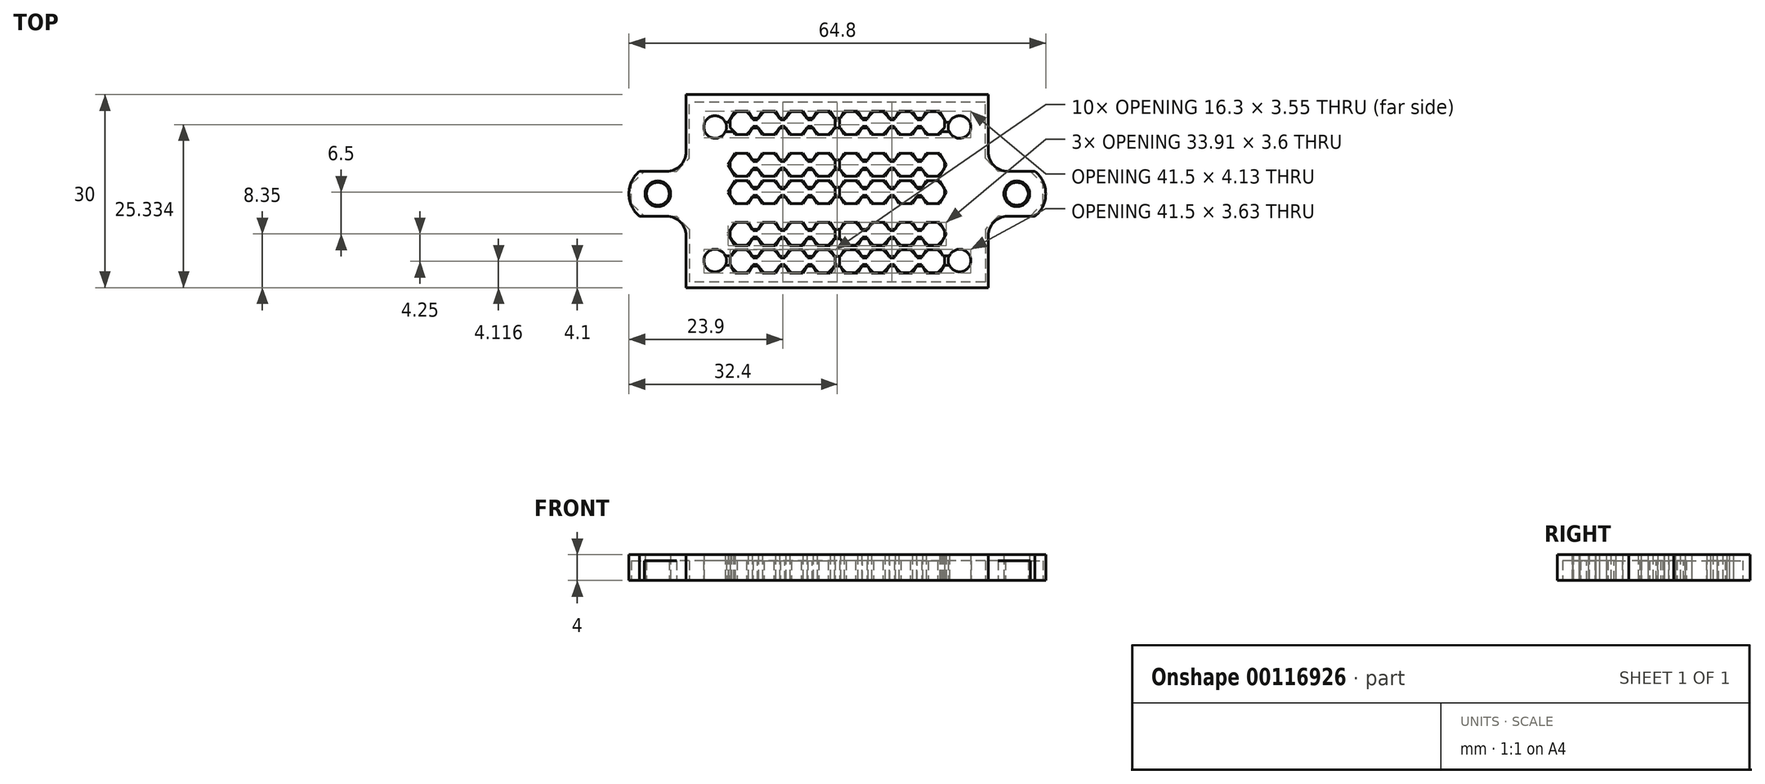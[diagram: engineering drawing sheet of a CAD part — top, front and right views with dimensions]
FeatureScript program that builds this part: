
annotation { "Feature Type Name" : "Feature", "Feature Type Description" : "" }
export const myFeature = defineFeature(function(context is Context, id is Id, definition is map)
    precondition{}
    {
        {
            var Q0;
            Q0=qCreatedBy(makeId("Top.planeOp"),FACE);
            var sketch = newSketch(context, id + "F0", { "sketchPlane" : qUnion([Q0])});
            skCircle(sketch, "E0", {"center": v(-19, 10.38) * mm, "radius": 1.77 * mm});
            skCircle(sketch, "E1.MirrorC", {"center": v(-19, -10.38) * mm, "radius": 1.77 * mm});
            skCircle(sketch, "E2.MirrorC", {"center": v(19, 10.38) * mm, "radius": 1.77 * mm});
            skCircle(sketch, "E3.MirrorC", {"center": v(19, -10.38) * mm, "radius": 1.77 * mm});
            skCircle(sketch, "E4", {"center": v(-27.9, 0) * mm, "radius": 1.77 * mm});
            skCircle(sketch, "E5.MirrorC", {"center": v(27.9, 0) * mm, "radius": 1.77 * mm});
            skLineSegment(sketch, "E6", {"start": v(-14.88, 11) * mm, "end": v(14.88, 11) * mm, "construction": true});
            skCircle(sketch, "E7.cCircle", {"center": v(-14.88, 11) * mm, "radius": 1.77 * mm, "construction": true});
            skLineSegment(sketch, "E7.0", {"start": v(-15.61, 12.77) * mm, "end": v(-14.14, 12.77) * mm});
            skLineSegment(sketch, "E7.1", {"start": v(-14.14, 12.78) * mm, "end": v(-13.1, 11.74) * mm});
            skLineSegment(sketch, "E7.2", {"start": v(-13.1, 11.74) * mm, "end": v(-13.1, 10.26) * mm});
            skLineSegment(sketch, "E7.3", {"start": v(-13.1, 10.26) * mm, "end": v(-14.14, 9.22) * mm});
            skLineSegment(sketch, "E7.4", {"start": v(-14.14, 9.22) * mm, "end": v(-15.61, 9.22) * mm});
            skLineSegment(sketch, "E7.5", {"start": v(-15.61, 9.22) * mm, "end": v(-16.65, 10.26) * mm});
            skLineSegment(sketch, "E7.6", {"start": v(-16.65, 10.26) * mm, "end": v(-16.65, 11.74) * mm});
            skLineSegment(sketch, "E7.7", {"start": v(-16.65, 11.74) * mm, "end": v(-15.61, 12.78) * mm});
            skPoint(sketch, "E7.0.midPoint", {"position": v(-14.88, 12.77) * mm});
            skLineSegment(sketch, "E8.1.0.0", {"start": v(-11.36, 12.77) * mm, "end": v(-9.89, 12.77) * mm});
            skLineSegment(sketch, "E8.1.0.1", {"start": v(-9.89, 12.78) * mm, "end": v(-8.85, 11.74) * mm});
            skLineSegment(sketch, "E8.1.0.2", {"start": v(-8.85, 11.74) * mm, "end": v(-8.85, 10.26) * mm});
            skLineSegment(sketch, "E8.1.0.3", {"start": v(-8.85, 10.26) * mm, "end": v(-9.89, 9.22) * mm});
            skLineSegment(sketch, "E8.1.0.4", {"start": v(-9.89, 9.22) * mm, "end": v(-11.36, 9.22) * mm});
            skLineSegment(sketch, "E8.1.0.5", {"start": v(-11.36, 9.22) * mm, "end": v(-12.4, 10.26) * mm});
            skLineSegment(sketch, "E8.1.0.6", {"start": v(-12.4, 10.26) * mm, "end": v(-12.4, 11.74) * mm});
            skLineSegment(sketch, "E8.1.0.7", {"start": v(-12.4, 11.74) * mm, "end": v(-11.36, 12.78) * mm});
            skLineSegment(sketch, "E8.2.0.0", {"start": v(-7.11, 12.77) * mm, "end": v(-5.64, 12.77) * mm});
            skLineSegment(sketch, "E8.2.0.1", {"start": v(-5.64, 12.78) * mm, "end": v(-4.6, 11.74) * mm});
            skLineSegment(sketch, "E8.2.0.2", {"start": v(-4.6, 11.74) * mm, "end": v(-4.6, 10.26) * mm});
            skLineSegment(sketch, "E8.2.0.3", {"start": v(-4.6, 10.26) * mm, "end": v(-5.64, 9.22) * mm});
            skLineSegment(sketch, "E8.2.0.4", {"start": v(-5.64, 9.22) * mm, "end": v(-7.11, 9.22) * mm});
            skLineSegment(sketch, "E8.2.0.5", {"start": v(-7.11, 9.22) * mm, "end": v(-8.15, 10.26) * mm});
            skLineSegment(sketch, "E8.2.0.6", {"start": v(-8.15, 10.26) * mm, "end": v(-8.15, 11.74) * mm});
            skLineSegment(sketch, "E8.2.0.7", {"start": v(-8.15, 11.74) * mm, "end": v(-7.11, 12.78) * mm});
            skLineSegment(sketch, "E8.3.0.0", {"start": v(-2.86, 12.77) * mm, "end": v(-1.39, 12.77) * mm});
            skLineSegment(sketch, "E8.3.0.1", {"start": v(-1.39, 12.78) * mm, "end": v(-0.35, 11.74) * mm});
            skLineSegment(sketch, "E8.3.0.2", {"start": v(-0.35, 11.74) * mm, "end": v(-0.35, 10.26) * mm});
            skLineSegment(sketch, "E8.3.0.3", {"start": v(-0.35, 10.26) * mm, "end": v(-1.39, 9.22) * mm});
            skLineSegment(sketch, "E8.3.0.4", {"start": v(-1.39, 9.22) * mm, "end": v(-2.86, 9.22) * mm});
            skLineSegment(sketch, "E8.3.0.5", {"start": v(-2.86, 9.22) * mm, "end": v(-3.9, 10.26) * mm});
            skLineSegment(sketch, "E8.3.0.6", {"start": v(-3.9, 10.26) * mm, "end": v(-3.9, 11.74) * mm});
            skLineSegment(sketch, "E8.3.0.7", {"start": v(-3.9, 11.74) * mm, "end": v(-2.86, 12.78) * mm});
            skLineSegment(sketch, "E8.4.0.0", {"start": v(1.39, 12.77) * mm, "end": v(2.86, 12.77) * mm});
            skLineSegment(sketch, "E8.4.0.1", {"start": v(2.86, 12.78) * mm, "end": v(3.9, 11.74) * mm});
            skLineSegment(sketch, "E8.4.0.2", {"start": v(3.9, 11.74) * mm, "end": v(3.9, 10.26) * mm});
            skLineSegment(sketch, "E8.4.0.3", {"start": v(3.9, 10.26) * mm, "end": v(2.86, 9.22) * mm});
            skLineSegment(sketch, "E8.4.0.4", {"start": v(2.86, 9.22) * mm, "end": v(1.39, 9.22) * mm});
            skLineSegment(sketch, "E8.4.0.5", {"start": v(1.39, 9.22) * mm, "end": v(0.35, 10.26) * mm});
            skLineSegment(sketch, "E8.4.0.6", {"start": v(0.35, 10.26) * mm, "end": v(0.35, 11.74) * mm});
            skLineSegment(sketch, "E8.4.0.7", {"start": v(0.35, 11.74) * mm, "end": v(1.39, 12.78) * mm});
            skLineSegment(sketch, "E8.5.0.0", {"start": v(5.64, 12.77) * mm, "end": v(7.11, 12.77) * mm});
            skLineSegment(sketch, "E8.5.0.1", {"start": v(7.11, 12.78) * mm, "end": v(8.15, 11.74) * mm});
            skLineSegment(sketch, "E8.5.0.2", {"start": v(8.15, 11.74) * mm, "end": v(8.15, 10.26) * mm});
            skLineSegment(sketch, "E8.5.0.3", {"start": v(8.15, 10.26) * mm, "end": v(7.11, 9.22) * mm});
            skLineSegment(sketch, "E8.5.0.4", {"start": v(7.11, 9.22) * mm, "end": v(5.64, 9.22) * mm});
            skLineSegment(sketch, "E8.5.0.5", {"start": v(5.64, 9.22) * mm, "end": v(4.6, 10.26) * mm});
            skLineSegment(sketch, "E8.5.0.6", {"start": v(4.6, 10.26) * mm, "end": v(4.6, 11.74) * mm});
            skLineSegment(sketch, "E8.5.0.7", {"start": v(4.6, 11.74) * mm, "end": v(5.64, 12.78) * mm});
            skLineSegment(sketch, "E8.6.0.0", {"start": v(9.89, 12.77) * mm, "end": v(11.36, 12.77) * mm});
            skLineSegment(sketch, "E8.6.0.1", {"start": v(11.36, 12.78) * mm, "end": v(12.4, 11.74) * mm});
            skLineSegment(sketch, "E8.6.0.2", {"start": v(12.4, 11.74) * mm, "end": v(12.4, 10.26) * mm});
            skLineSegment(sketch, "E8.6.0.3", {"start": v(12.4, 10.26) * mm, "end": v(11.36, 9.22) * mm});
            skLineSegment(sketch, "E8.6.0.4", {"start": v(11.36, 9.22) * mm, "end": v(9.89, 9.22) * mm});
            skLineSegment(sketch, "E8.6.0.5", {"start": v(9.89, 9.22) * mm, "end": v(8.85, 10.26) * mm});
            skLineSegment(sketch, "E8.6.0.6", {"start": v(8.85, 10.26) * mm, "end": v(8.85, 11.74) * mm});
            skLineSegment(sketch, "E8.6.0.7", {"start": v(8.85, 11.74) * mm, "end": v(9.89, 12.78) * mm});
            skLineSegment(sketch, "E8.7.0.0", {"start": v(14.14, 12.77) * mm, "end": v(15.61, 12.77) * mm});
            skLineSegment(sketch, "E8.7.0.1", {"start": v(15.61, 12.78) * mm, "end": v(16.65, 11.74) * mm});
            skLineSegment(sketch, "E8.7.0.2", {"start": v(16.65, 11.74) * mm, "end": v(16.65, 10.26) * mm});
            skLineSegment(sketch, "E8.7.0.3", {"start": v(16.65, 10.26) * mm, "end": v(15.61, 9.22) * mm});
            skLineSegment(sketch, "E8.7.0.4", {"start": v(15.61, 9.22) * mm, "end": v(14.14, 9.22) * mm});
            skLineSegment(sketch, "E8.7.0.5", {"start": v(14.14, 9.22) * mm, "end": v(13.1, 10.26) * mm});
            skLineSegment(sketch, "E8.7.0.6", {"start": v(13.1, 10.26) * mm, "end": v(13.1, 11.74) * mm});
            skLineSegment(sketch, "E8.7.0.7", {"start": v(13.1, 11.74) * mm, "end": v(14.14, 12.78) * mm});
            skLineSegment(sketch, "E8.direction1", {"start": v(-15.61, 12.77) * mm, "end": v(-11.36, 12.77) * mm, "construction": true});
            skPoint(sketch, "E9.0.1.0", {"position": v(-14.88, 2.02) * mm});
            skLineSegment(sketch, "E9.0.1.1", {"start": v(16.65, -0.49) * mm, "end": v(15.61, -1.53) * mm});
            skLineSegment(sketch, "E9.0.1.2", {"start": v(8.15, -0.49) * mm, "end": v(7.11, -1.53) * mm});
            skLineSegment(sketch, "E9.0.1.3", {"start": v(7.11, 2.03) * mm, "end": v(8.15, 0.99) * mm});
            skLineSegment(sketch, "E9.0.1.4", {"start": v(-2.86, 2.02) * mm, "end": v(-1.39, 2.02) * mm});
            skLineSegment(sketch, "E9.0.1.5", {"start": v(3.9, -0.49) * mm, "end": v(2.86, -1.53) * mm});
            skLineSegment(sketch, "E9.0.1.6", {"start": v(-4.6, -0.49) * mm, "end": v(-5.64, -1.53) * mm});
            skLineSegment(sketch, "E9.0.1.7", {"start": v(-9.89, -1.53) * mm, "end": v(-11.36, -1.53) * mm});
            skLineSegment(sketch, "E9.0.1.8", {"start": v(5.64, 2.02) * mm, "end": v(7.11, 2.02) * mm});
            skLineSegment(sketch, "E9.0.1.9", {"start": v(8.85, -0.49) * mm, "end": v(8.85, 0.99) * mm});
            skLineSegment(sketch, "E9.0.1.10", {"start": v(14.14, -1.53) * mm, "end": v(13.1, -0.49) * mm});
            skLineSegment(sketch, "E9.0.1.11", {"start": v(0.35, -0.49) * mm, "end": v(0.35, 0.99) * mm});
            skLineSegment(sketch, "E9.0.1.12", {"start": v(-7.11, 2.02) * mm, "end": v(-5.64, 2.02) * mm});
            skLineSegment(sketch, "E9.0.1.13", {"start": v(-16.65, 0.99) * mm, "end": v(-15.61, 2.02) * mm});
            skLineSegment(sketch, "E9.0.1.14", {"start": v(4.6, 0.99) * mm, "end": v(5.64, 2.02) * mm});
            skLineSegment(sketch, "E9.0.1.15", {"start": v(12.4, 0.99) * mm, "end": v(12.4, -0.49) * mm});
            skLineSegment(sketch, "E9.0.1.16", {"start": v(3.9, 0.99) * mm, "end": v(3.9, -0.49) * mm});
            skLineSegment(sketch, "E9.0.1.17", {"start": v(-8.85, 0.99) * mm, "end": v(-8.85, -0.49) * mm});
            skLineSegment(sketch, "E9.0.1.18", {"start": v(15.61, 2.03) * mm, "end": v(16.65, 0.99) * mm});
            skLineSegment(sketch, "E9.0.1.19", {"start": v(-0.35, -0.49) * mm, "end": v(-1.39, -1.53) * mm});
            skLineSegment(sketch, "E9.0.1.20", {"start": v(1.39, 2.02) * mm, "end": v(2.86, 2.02) * mm});
            skLineSegment(sketch, "E9.0.1.21", {"start": v(16.65, 0.99) * mm, "end": v(16.65, -0.49) * mm});
            skLineSegment(sketch, "E9.0.1.22", {"start": v(9.89, 2.02) * mm, "end": v(11.36, 2.02) * mm});
            skLineSegment(sketch, "E9.0.1.23", {"start": v(2.86, 2.03) * mm, "end": v(3.9, 0.99) * mm});
            skLineSegment(sketch, "E9.0.1.24", {"start": v(13.1, 0.99) * mm, "end": v(14.14, 2.02) * mm});
            skLineSegment(sketch, "E9.0.1.25", {"start": v(15.61, -1.53) * mm, "end": v(14.14, -1.53) * mm});
            skLineSegment(sketch, "E9.0.1.26", {"start": v(-1.39, -1.53) * mm, "end": v(-2.86, -1.53) * mm});
            skLineSegment(sketch, "E9.0.1.27", {"start": v(-0.35, 0.99) * mm, "end": v(-0.35, -0.49) * mm});
            skLineSegment(sketch, "E9.0.1.28", {"start": v(11.36, 2.03) * mm, "end": v(12.4, 0.99) * mm});
            skLineSegment(sketch, "E9.0.1.29", {"start": v(-3.9, -0.49) * mm, "end": v(-3.9, 0.99) * mm});
            skLineSegment(sketch, "E9.0.1.30", {"start": v(-15.61, -1.53) * mm, "end": v(-16.65, -0.49) * mm});
            skLineSegment(sketch, "E9.0.1.31", {"start": v(-16.65, -0.49) * mm, "end": v(-16.65, 0.99) * mm});
            skLineSegment(sketch, "E9.0.1.32", {"start": v(-5.64, 2.03) * mm, "end": v(-4.6, 0.99) * mm});
            skLineSegment(sketch, "E9.0.1.33", {"start": v(-9.89, 2.03) * mm, "end": v(-8.85, 0.99) * mm});
            skLineSegment(sketch, "E9.0.1.34", {"start": v(-3.9, 0.99) * mm, "end": v(-2.86, 2.02) * mm});
            skLineSegment(sketch, "E9.0.1.35", {"start": v(14.14, 2.02) * mm, "end": v(15.61, 2.02) * mm});
            skLineSegment(sketch, "E9.0.1.36", {"start": v(8.15, 0.99) * mm, "end": v(8.15, -0.49) * mm});
            skLineSegment(sketch, "E9.0.1.37", {"start": v(12.4, -0.49) * mm, "end": v(11.36, -1.53) * mm});
            skLineSegment(sketch, "E9.0.1.38", {"start": v(-1.39, 2.03) * mm, "end": v(-0.35, 0.99) * mm});
            skLineSegment(sketch, "E9.0.1.39", {"start": v(7.11, -1.53) * mm, "end": v(5.64, -1.53) * mm});
            skLineSegment(sketch, "E9.0.1.40", {"start": v(-14.14, 2.03) * mm, "end": v(-13.1, 0.99) * mm});
            skLineSegment(sketch, "E9.0.1.41", {"start": v(-4.6, 0.99) * mm, "end": v(-4.6, -0.49) * mm});
            skLineSegment(sketch, "E9.0.1.42", {"start": v(11.36, -1.53) * mm, "end": v(9.89, -1.53) * mm});
            skLineSegment(sketch, "E9.0.1.43", {"start": v(-5.64, -1.53) * mm, "end": v(-7.11, -1.53) * mm});
            skLineSegment(sketch, "E9.0.1.44", {"start": v(2.86, -1.53) * mm, "end": v(1.39, -1.53) * mm});
            skLineSegment(sketch, "E9.0.1.45", {"start": v(-8.15, -0.49) * mm, "end": v(-8.15, 0.99) * mm});
            skLineSegment(sketch, "E9.0.1.46", {"start": v(-2.86, -1.53) * mm, "end": v(-3.9, -0.49) * mm});
            skLineSegment(sketch, "E9.0.1.47", {"start": v(8.85, 0.99) * mm, "end": v(9.89, 2.02) * mm});
            skLineSegment(sketch, "E9.0.1.48", {"start": v(13.1, -0.49) * mm, "end": v(13.1, 0.99) * mm});
            skLineSegment(sketch, "E9.0.1.49", {"start": v(0.35, 0.99) * mm, "end": v(1.39, 2.02) * mm});
            skLineSegment(sketch, "E9.0.1.50", {"start": v(4.6, -0.49) * mm, "end": v(4.6, 0.99) * mm});
            skLineSegment(sketch, "E9.0.1.51", {"start": v(-8.15, 0.99) * mm, "end": v(-7.11, 2.02) * mm});
            skLineSegment(sketch, "E9.0.1.52", {"start": v(-13.1, 0.99) * mm, "end": v(-13.1, -0.49) * mm});
            skLineSegment(sketch, "E9.0.1.53", {"start": v(-7.11, -1.53) * mm, "end": v(-8.15, -0.49) * mm});
            skLineSegment(sketch, "E9.0.1.54", {"start": v(-15.61, 2.02) * mm, "end": v(-14.14, 2.02) * mm});
            skLineSegment(sketch, "E9.0.1.55", {"start": v(-12.4, 0.99) * mm, "end": v(-11.36, 2.02) * mm});
            skLineSegment(sketch, "E9.0.1.56", {"start": v(-11.36, 2.02) * mm, "end": v(-9.89, 2.02) * mm});
            skLineSegment(sketch, "E9.0.1.57", {"start": v(-14.14, -1.53) * mm, "end": v(-15.61, -1.53) * mm});
            skLineSegment(sketch, "E9.0.1.58", {"start": v(-8.85, -0.49) * mm, "end": v(-9.89, -1.53) * mm});
            skLineSegment(sketch, "E9.0.1.59", {"start": v(-13.1, -0.49) * mm, "end": v(-14.14, -1.53) * mm});
            skLineSegment(sketch, "E9.0.1.60", {"start": v(9.89, -1.53) * mm, "end": v(8.85, -0.49) * mm});
            skLineSegment(sketch, "E9.0.1.61", {"start": v(1.39, -1.53) * mm, "end": v(0.35, -0.49) * mm});
            skLineSegment(sketch, "E9.0.1.62", {"start": v(-11.36, -1.53) * mm, "end": v(-12.4, -0.49) * mm});
            skLineSegment(sketch, "E9.0.1.63", {"start": v(5.64, -1.53) * mm, "end": v(4.6, -0.49) * mm});
            skLineSegment(sketch, "E9.0.1.64", {"start": v(-12.4, -0.49) * mm, "end": v(-12.4, 0.99) * mm});
            skPoint(sketch, "E9.0.2.0", {"position": v(-14.88, -8.73) * mm});
            skLineSegment(sketch, "E9.0.2.1", {"start": v(16.65, -11.24) * mm, "end": v(15.61, -12.28) * mm});
            skLineSegment(sketch, "E9.0.2.2", {"start": v(8.15, -11.24) * mm, "end": v(7.11, -12.28) * mm});
            skLineSegment(sketch, "E9.0.2.3", {"start": v(7.11, -8.72) * mm, "end": v(8.15, -9.76) * mm});
            skLineSegment(sketch, "E9.0.2.4", {"start": v(-2.86, -8.73) * mm, "end": v(-1.39, -8.73) * mm});
            skLineSegment(sketch, "E9.0.2.5", {"start": v(3.9, -11.24) * mm, "end": v(2.86, -12.28) * mm});
            skLineSegment(sketch, "E9.0.2.6", {"start": v(-4.6, -11.24) * mm, "end": v(-5.64, -12.28) * mm});
            skLineSegment(sketch, "E9.0.2.7", {"start": v(-9.89, -12.28) * mm, "end": v(-11.36, -12.28) * mm});
            skLineSegment(sketch, "E9.0.2.8", {"start": v(5.64, -8.73) * mm, "end": v(7.11, -8.73) * mm});
            skLineSegment(sketch, "E9.0.2.9", {"start": v(8.85, -11.24) * mm, "end": v(8.85, -9.76) * mm});
            skLineSegment(sketch, "E9.0.2.10", {"start": v(14.14, -12.28) * mm, "end": v(13.1, -11.24) * mm});
            skLineSegment(sketch, "E9.0.2.11", {"start": v(0.35, -11.24) * mm, "end": v(0.35, -9.76) * mm});
            skLineSegment(sketch, "E9.0.2.12", {"start": v(-7.11, -8.73) * mm, "end": v(-5.64, -8.73) * mm});
            skLineSegment(sketch, "E9.0.2.13", {"start": v(-16.65, -9.76) * mm, "end": v(-15.61, -8.73) * mm});
            skLineSegment(sketch, "E9.0.2.14", {"start": v(4.6, -9.76) * mm, "end": v(5.64, -8.73) * mm});
            skLineSegment(sketch, "E9.0.2.15", {"start": v(12.4, -9.76) * mm, "end": v(12.4, -11.24) * mm});
            skLineSegment(sketch, "E9.0.2.16", {"start": v(3.9, -9.76) * mm, "end": v(3.9, -11.24) * mm});
            skLineSegment(sketch, "E9.0.2.17", {"start": v(-8.85, -9.76) * mm, "end": v(-8.85, -11.24) * mm});
            skLineSegment(sketch, "E9.0.2.18", {"start": v(15.61, -8.72) * mm, "end": v(16.65, -9.76) * mm});
            skLineSegment(sketch, "E9.0.2.19", {"start": v(-0.35, -11.24) * mm, "end": v(-1.39, -12.28) * mm});
            skLineSegment(sketch, "E9.0.2.20", {"start": v(1.39, -8.73) * mm, "end": v(2.86, -8.73) * mm});
            skLineSegment(sketch, "E9.0.2.21", {"start": v(16.65, -9.76) * mm, "end": v(16.65, -11.24) * mm});
            skLineSegment(sketch, "E9.0.2.22", {"start": v(9.89, -8.73) * mm, "end": v(11.36, -8.73) * mm});
            skLineSegment(sketch, "E9.0.2.23", {"start": v(2.86, -8.72) * mm, "end": v(3.9, -9.76) * mm});
            skLineSegment(sketch, "E9.0.2.24", {"start": v(13.1, -9.76) * mm, "end": v(14.14, -8.73) * mm});
            skLineSegment(sketch, "E9.0.2.25", {"start": v(15.61, -12.28) * mm, "end": v(14.14, -12.28) * mm});
            skLineSegment(sketch, "E9.0.2.26", {"start": v(-1.39, -12.28) * mm, "end": v(-2.86, -12.28) * mm});
            skLineSegment(sketch, "E9.0.2.27", {"start": v(-0.35, -9.76) * mm, "end": v(-0.35, -11.24) * mm});
            skLineSegment(sketch, "E9.0.2.28", {"start": v(11.36, -8.72) * mm, "end": v(12.4, -9.76) * mm});
            skLineSegment(sketch, "E9.0.2.29", {"start": v(-3.9, -11.24) * mm, "end": v(-3.9, -9.76) * mm});
            skLineSegment(sketch, "E9.0.2.30", {"start": v(-15.61, -12.28) * mm, "end": v(-16.65, -11.24) * mm});
            skLineSegment(sketch, "E9.0.2.31", {"start": v(-16.65, -11.24) * mm, "end": v(-16.65, -9.76) * mm});
            skLineSegment(sketch, "E9.0.2.32", {"start": v(-5.64, -8.72) * mm, "end": v(-4.6, -9.76) * mm});
            skLineSegment(sketch, "E9.0.2.33", {"start": v(-9.89, -8.72) * mm, "end": v(-8.85, -9.76) * mm});
            skLineSegment(sketch, "E9.0.2.34", {"start": v(-3.9, -9.76) * mm, "end": v(-2.86, -8.73) * mm});
            skLineSegment(sketch, "E9.0.2.35", {"start": v(14.14, -8.73) * mm, "end": v(15.61, -8.73) * mm});
            skLineSegment(sketch, "E9.0.2.36", {"start": v(8.15, -9.76) * mm, "end": v(8.15, -11.24) * mm});
            skLineSegment(sketch, "E9.0.2.37", {"start": v(12.4, -11.24) * mm, "end": v(11.36, -12.28) * mm});
            skLineSegment(sketch, "E9.0.2.38", {"start": v(-1.39, -8.72) * mm, "end": v(-0.35, -9.76) * mm});
            skLineSegment(sketch, "E9.0.2.39", {"start": v(7.11, -12.28) * mm, "end": v(5.64, -12.28) * mm});
            skLineSegment(sketch, "E9.0.2.40", {"start": v(-14.14, -8.72) * mm, "end": v(-13.1, -9.76) * mm});
            skLineSegment(sketch, "E9.0.2.41", {"start": v(-4.6, -9.76) * mm, "end": v(-4.6, -11.24) * mm});
            skLineSegment(sketch, "E9.0.2.42", {"start": v(11.36, -12.28) * mm, "end": v(9.89, -12.28) * mm});
            skLineSegment(sketch, "E9.0.2.43", {"start": v(-5.64, -12.28) * mm, "end": v(-7.11, -12.28) * mm});
            skLineSegment(sketch, "E9.0.2.44", {"start": v(2.86, -12.28) * mm, "end": v(1.39, -12.28) * mm});
            skLineSegment(sketch, "E9.0.2.45", {"start": v(-8.15, -11.24) * mm, "end": v(-8.15, -9.76) * mm});
            skLineSegment(sketch, "E9.0.2.46", {"start": v(-2.86, -12.28) * mm, "end": v(-3.9, -11.24) * mm});
            skLineSegment(sketch, "E9.0.2.47", {"start": v(8.85, -9.76) * mm, "end": v(9.89, -8.73) * mm});
            skLineSegment(sketch, "E9.0.2.48", {"start": v(13.1, -11.24) * mm, "end": v(13.1, -9.76) * mm});
            skLineSegment(sketch, "E9.0.2.49", {"start": v(0.35, -9.76) * mm, "end": v(1.39, -8.73) * mm});
            skLineSegment(sketch, "E9.0.2.50", {"start": v(4.6, -11.24) * mm, "end": v(4.6, -9.76) * mm});
            skLineSegment(sketch, "E9.0.2.51", {"start": v(-8.15, -9.76) * mm, "end": v(-7.11, -8.73) * mm});
            skLineSegment(sketch, "E9.0.2.52", {"start": v(-13.1, -9.76) * mm, "end": v(-13.1, -11.24) * mm});
            skLineSegment(sketch, "E9.0.2.53", {"start": v(-7.11, -12.28) * mm, "end": v(-8.15, -11.24) * mm});
            skLineSegment(sketch, "E9.0.2.54", {"start": v(-15.61, -8.73) * mm, "end": v(-14.14, -8.73) * mm});
            skLineSegment(sketch, "E9.0.2.55", {"start": v(-12.4, -9.76) * mm, "end": v(-11.36, -8.73) * mm});
            skLineSegment(sketch, "E9.0.2.56", {"start": v(-11.36, -8.73) * mm, "end": v(-9.89, -8.73) * mm});
            skLineSegment(sketch, "E9.0.2.57", {"start": v(-14.14, -12.28) * mm, "end": v(-15.61, -12.28) * mm});
            skLineSegment(sketch, "E9.0.2.58", {"start": v(-8.85, -11.24) * mm, "end": v(-9.89, -12.28) * mm});
            skLineSegment(sketch, "E9.0.2.59", {"start": v(-13.1, -11.24) * mm, "end": v(-14.14, -12.28) * mm});
            skLineSegment(sketch, "E9.0.2.60", {"start": v(9.89, -12.28) * mm, "end": v(8.85, -11.24) * mm});
            skLineSegment(sketch, "E9.0.2.61", {"start": v(1.39, -12.28) * mm, "end": v(0.35, -11.24) * mm});
            skLineSegment(sketch, "E9.0.2.62", {"start": v(-11.36, -12.28) * mm, "end": v(-12.4, -11.24) * mm});
            skLineSegment(sketch, "E9.0.2.63", {"start": v(5.64, -12.28) * mm, "end": v(4.6, -11.24) * mm});
            skLineSegment(sketch, "E9.0.2.64", {"start": v(-12.4, -11.24) * mm, "end": v(-12.4, -9.76) * mm});
            skLineSegment(sketch, "E9.direction1", {"start": v(-15.61, 9.22) * mm, "end": v(9.39, 9.22) * mm, "construction": true});
            skLineSegment(sketch, "E9.direction2", {"start": v(-15.61, 9.22) * mm, "end": v(-15.61, -1.53) * mm, "construction": true});
            skPoint(sketch, "E10.0.1.0", {"position": v(-14.88, -4.48) * mm});
            skPoint(sketch, "E10.0.1.1", {"position": v(-14.88, 6.27) * mm});
            skLineSegment(sketch, "E10.0.1.2", {"start": v(-15.61, 6.27) * mm, "end": v(-14.14, 6.27) * mm});
            skLineSegment(sketch, "E10.0.1.3", {"start": v(-13.1, 5.24) * mm, "end": v(-13.1, 3.76) * mm});
            skLineSegment(sketch, "E10.0.1.4", {"start": v(-7.11, -8.03) * mm, "end": v(-8.15, -6.99) * mm});
            skLineSegment(sketch, "E10.0.1.5", {"start": v(-7.11, 2.72) * mm, "end": v(-8.15, 3.76) * mm});
            skLineSegment(sketch, "E10.0.1.6", {"start": v(12.4, 3.76) * mm, "end": v(11.36, 2.72) * mm});
            skLineSegment(sketch, "E10.0.1.7", {"start": v(16.65, 5.24) * mm, "end": v(16.65, 3.76) * mm});
            skLineSegment(sketch, "E10.0.1.8", {"start": v(3.9, -6.99) * mm, "end": v(2.86, -8.03) * mm});
            skLineSegment(sketch, "E10.0.1.9", {"start": v(12.4, -6.99) * mm, "end": v(11.36, -8.03) * mm});
            skLineSegment(sketch, "E10.0.1.10", {"start": v(16.65, -5.51) * mm, "end": v(16.65, -6.99) * mm});
            skLineSegment(sketch, "E10.0.1.11", {"start": v(8.15, -6.99) * mm, "end": v(7.11, -8.03) * mm});
            skLineSegment(sketch, "E10.0.1.12", {"start": v(8.15, 3.76) * mm, "end": v(7.11, 2.72) * mm});
            skLineSegment(sketch, "E10.0.1.13", {"start": v(15.61, 6.28) * mm, "end": v(16.65, 5.24) * mm});
            skLineSegment(sketch, "E10.0.1.14", {"start": v(4.6, -6.99) * mm, "end": v(4.6, -5.51) * mm});
            skLineSegment(sketch, "E10.0.1.15", {"start": v(-3.9, -5.51) * mm, "end": v(-2.86, -4.48) * mm});
            skLineSegment(sketch, "E10.0.1.16", {"start": v(15.61, -4.47) * mm, "end": v(16.65, -5.51) * mm});
            skLineSegment(sketch, "E10.0.1.17", {"start": v(3.9, 3.76) * mm, "end": v(2.86, 2.72) * mm});
            skLineSegment(sketch, "E10.0.1.18", {"start": v(14.14, -4.48) * mm, "end": v(15.61, -4.48) * mm});
            skLineSegment(sketch, "E10.0.1.19", {"start": v(-0.35, -6.99) * mm, "end": v(-1.39, -8.03) * mm});
            skLineSegment(sketch, "E10.0.1.20", {"start": v(7.11, -4.47) * mm, "end": v(8.15, -5.51) * mm});
            skLineSegment(sketch, "E10.0.1.21", {"start": v(-8.15, 5.24) * mm, "end": v(-7.11, 6.27) * mm});
            skLineSegment(sketch, "E10.0.1.22", {"start": v(-0.35, 3.76) * mm, "end": v(-1.39, 2.72) * mm});
            skLineSegment(sketch, "E10.0.1.23", {"start": v(7.11, 6.28) * mm, "end": v(8.15, 5.24) * mm});
            skLineSegment(sketch, "E10.0.1.24", {"start": v(-8.15, -5.51) * mm, "end": v(-7.11, -4.48) * mm});
            skLineSegment(sketch, "E10.0.1.25", {"start": v(14.14, 6.27) * mm, "end": v(15.61, 6.27) * mm});
            skLineSegment(sketch, "E10.0.1.26", {"start": v(4.6, 3.76) * mm, "end": v(4.6, 5.24) * mm});
            skLineSegment(sketch, "E10.0.1.27", {"start": v(-3.9, 5.24) * mm, "end": v(-2.86, 6.27) * mm});
            skLineSegment(sketch, "E10.0.1.28", {"start": v(-5.64, 6.28) * mm, "end": v(-4.6, 5.24) * mm});
            skLineSegment(sketch, "E10.0.1.29", {"start": v(13.1, 3.76) * mm, "end": v(13.1, 5.24) * mm});
            skLineSegment(sketch, "E10.0.1.30", {"start": v(13.1, -6.99) * mm, "end": v(13.1, -5.51) * mm});
            skLineSegment(sketch, "E10.0.1.31", {"start": v(12.4, -5.51) * mm, "end": v(12.4, -6.99) * mm});
            skLineSegment(sketch, "E10.0.1.32", {"start": v(5.64, 2.72) * mm, "end": v(4.6, 3.76) * mm});
            skLineSegment(sketch, "E10.0.1.33", {"start": v(5.64, -8.03) * mm, "end": v(4.6, -6.99) * mm});
            skLineSegment(sketch, "E10.0.1.34", {"start": v(8.85, 5.24) * mm, "end": v(9.89, 6.27) * mm});
            skLineSegment(sketch, "E10.0.1.35", {"start": v(12.4, 5.24) * mm, "end": v(12.4, 3.76) * mm});
            skLineSegment(sketch, "E10.0.1.36", {"start": v(-8.15, -6.99) * mm, "end": v(-8.15, -5.51) * mm});
            skLineSegment(sketch, "E10.0.1.37", {"start": v(0.35, -5.51) * mm, "end": v(1.39, -4.48) * mm});
            skLineSegment(sketch, "E10.0.1.38", {"start": v(-8.85, -5.51) * mm, "end": v(-8.85, -6.99) * mm});
            skLineSegment(sketch, "E10.0.1.39", {"start": v(-9.89, 6.28) * mm, "end": v(-8.85, 5.24) * mm});
            skLineSegment(sketch, "E10.0.1.40", {"start": v(-8.85, 5.24) * mm, "end": v(-8.85, 3.76) * mm});
            skLineSegment(sketch, "E10.0.1.41", {"start": v(-16.65, -6.99) * mm, "end": v(-16.65, -5.51) * mm});
            skLineSegment(sketch, "E10.0.1.42", {"start": v(16.65, -6.99) * mm, "end": v(15.61, -8.03) * mm});
            skLineSegment(sketch, "E10.0.1.43", {"start": v(0.35, 5.24) * mm, "end": v(1.39, 6.27) * mm});
            skLineSegment(sketch, "E10.0.1.44", {"start": v(16.65, 3.76) * mm, "end": v(15.61, 2.72) * mm});
            skLineSegment(sketch, "E10.0.1.45", {"start": v(-9.89, -4.47) * mm, "end": v(-8.85, -5.51) * mm});
            skLineSegment(sketch, "E10.0.1.46", {"start": v(-12.4, -6.99) * mm, "end": v(-12.4, -5.51) * mm});
            skLineSegment(sketch, "E10.0.1.47", {"start": v(-5.64, -4.47) * mm, "end": v(-4.6, -5.51) * mm});
            skLineSegment(sketch, "E10.0.1.48", {"start": v(-12.4, 3.76) * mm, "end": v(-12.4, 5.24) * mm});
            skLineSegment(sketch, "E10.0.1.49", {"start": v(-3.9, 3.76) * mm, "end": v(-3.9, 5.24) * mm});
            skLineSegment(sketch, "E10.0.1.50", {"start": v(-16.65, -5.51) * mm, "end": v(-15.61, -4.48) * mm});
            skLineSegment(sketch, "E10.0.1.51", {"start": v(-8.15, 3.76) * mm, "end": v(-8.15, 5.24) * mm});
            skLineSegment(sketch, "E10.0.1.52", {"start": v(1.39, -8.03) * mm, "end": v(0.35, -6.99) * mm});
            skLineSegment(sketch, "E10.0.1.53", {"start": v(-16.65, 5.24) * mm, "end": v(-15.61, 6.27) * mm});
            skLineSegment(sketch, "E10.0.1.54", {"start": v(9.89, -8.03) * mm, "end": v(8.85, -6.99) * mm});
            skLineSegment(sketch, "E10.0.1.55", {"start": v(11.36, -4.47) * mm, "end": v(12.4, -5.51) * mm});
            skLineSegment(sketch, "E10.0.1.56", {"start": v(2.86, -8.03) * mm, "end": v(1.39, -8.03) * mm});
            skLineSegment(sketch, "E10.0.1.57", {"start": v(-7.11, -4.48) * mm, "end": v(-5.64, -4.48) * mm});
            skLineSegment(sketch, "E10.0.1.58", {"start": v(2.86, 2.72) * mm, "end": v(1.39, 2.72) * mm});
            skLineSegment(sketch, "E10.0.1.59", {"start": v(-3.9, -6.99) * mm, "end": v(-3.9, -5.51) * mm});
            skLineSegment(sketch, "E10.0.1.60", {"start": v(1.39, 2.72) * mm, "end": v(0.35, 3.76) * mm});
            skLineSegment(sketch, "E10.0.1.61", {"start": v(9.89, 2.72) * mm, "end": v(8.85, 3.76) * mm});
            skLineSegment(sketch, "E10.0.1.62", {"start": v(11.36, 6.28) * mm, "end": v(12.4, 5.24) * mm});
            skLineSegment(sketch, "E10.0.1.63", {"start": v(-7.11, 6.27) * mm, "end": v(-5.64, 6.27) * mm});
            skLineSegment(sketch, "E10.0.1.64", {"start": v(-13.1, -6.99) * mm, "end": v(-14.14, -8.03) * mm});
            skLineSegment(sketch, "E10.0.1.65", {"start": v(-5.64, -8.03) * mm, "end": v(-7.11, -8.03) * mm});
            skLineSegment(sketch, "E10.0.1.66", {"start": v(-0.35, 5.24) * mm, "end": v(-0.35, 3.76) * mm});
            skLineSegment(sketch, "E10.0.1.67", {"start": v(-0.35, -5.51) * mm, "end": v(-0.35, -6.99) * mm});
            skLineSegment(sketch, "E10.0.1.68", {"start": v(0.35, -6.99) * mm, "end": v(0.35, -5.51) * mm});
            skLineSegment(sketch, "E10.0.1.69", {"start": v(-13.1, 3.76) * mm, "end": v(-14.14, 2.72) * mm});
            skLineSegment(sketch, "E10.0.1.70", {"start": v(-5.64, 2.72) * mm, "end": v(-7.11, 2.72) * mm});
            skLineSegment(sketch, "E10.0.1.71", {"start": v(0.35, 3.76) * mm, "end": v(0.35, 5.24) * mm});
            skLineSegment(sketch, "E10.0.1.72", {"start": v(-15.61, -4.48) * mm, "end": v(-14.14, -4.48) * mm});
            skLineSegment(sketch, "E10.0.1.73", {"start": v(-9.89, -8.03) * mm, "end": v(-11.36, -8.03) * mm});
            skLineSegment(sketch, "E10.0.1.74", {"start": v(-4.6, 5.24) * mm, "end": v(-4.6, 3.76) * mm});
            skLineSegment(sketch, "E10.0.1.75", {"start": v(-11.36, 6.27) * mm, "end": v(-9.89, 6.27) * mm});
            skLineSegment(sketch, "E10.0.1.76", {"start": v(13.1, 5.24) * mm, "end": v(14.14, 6.27) * mm});
            skLineSegment(sketch, "E10.0.1.77", {"start": v(11.36, 2.72) * mm, "end": v(9.89, 2.72) * mm});
            skLineSegment(sketch, "E10.0.1.78", {"start": v(-12.4, -5.51) * mm, "end": v(-11.36, -4.48) * mm});
            skLineSegment(sketch, "E10.0.1.79", {"start": v(-4.6, 3.76) * mm, "end": v(-5.64, 2.72) * mm});
            skLineSegment(sketch, "E10.0.1.80", {"start": v(8.85, 3.76) * mm, "end": v(8.85, 5.24) * mm});
            skLineSegment(sketch, "E10.0.1.81", {"start": v(-14.14, 2.72) * mm, "end": v(-15.61, 2.72) * mm});
            skLineSegment(sketch, "E10.0.1.82", {"start": v(-13.1, -5.51) * mm, "end": v(-13.1, -6.99) * mm});
            skLineSegment(sketch, "E10.0.1.83", {"start": v(8.15, 5.24) * mm, "end": v(8.15, 3.76) * mm});
            skLineSegment(sketch, "E10.0.1.84", {"start": v(-4.6, -6.99) * mm, "end": v(-5.64, -8.03) * mm});
            skLineSegment(sketch, "E10.0.1.85", {"start": v(-1.39, 2.72) * mm, "end": v(-2.86, 2.72) * mm});
            skLineSegment(sketch, "E10.0.1.86", {"start": v(-1.39, 6.28) * mm, "end": v(-0.35, 5.24) * mm});
            skLineSegment(sketch, "E10.0.1.87", {"start": v(2.86, 6.28) * mm, "end": v(3.9, 5.24) * mm});
            skLineSegment(sketch, "E10.0.1.88", {"start": v(-8.85, 3.76) * mm, "end": v(-9.89, 2.72) * mm});
            skLineSegment(sketch, "E10.0.1.89", {"start": v(14.14, 2.72) * mm, "end": v(13.1, 3.76) * mm});
            skLineSegment(sketch, "E10.0.1.90", {"start": v(-1.39, -4.47) * mm, "end": v(-0.35, -5.51) * mm});
            skLineSegment(sketch, "E10.0.1.91", {"start": v(-8.85, -6.99) * mm, "end": v(-9.89, -8.03) * mm});
            skLineSegment(sketch, "E10.0.1.92", {"start": v(7.11, 2.72) * mm, "end": v(5.64, 2.72) * mm});
            skLineSegment(sketch, "E10.0.1.93", {"start": v(15.61, 2.72) * mm, "end": v(14.14, 2.72) * mm});
            skLineSegment(sketch, "E10.0.1.94", {"start": v(-2.86, 6.27) * mm, "end": v(-1.39, 6.27) * mm});
            skLineSegment(sketch, "E10.0.1.95", {"start": v(-1.39, -8.03) * mm, "end": v(-2.86, -8.03) * mm});
            skLineSegment(sketch, "E10.0.1.96", {"start": v(-11.36, -4.48) * mm, "end": v(-9.89, -4.48) * mm});
            skLineSegment(sketch, "E10.0.1.97", {"start": v(1.39, -4.48) * mm, "end": v(2.86, -4.48) * mm});
            skLineSegment(sketch, "E10.0.1.98", {"start": v(5.64, 6.27) * mm, "end": v(7.11, 6.27) * mm});
            skLineSegment(sketch, "E10.0.1.99", {"start": v(-9.89, 2.72) * mm, "end": v(-11.36, 2.72) * mm});
            skLineSegment(sketch, "E10.0.1.100", {"start": v(-12.4, 5.24) * mm, "end": v(-11.36, 6.27) * mm});
            skLineSegment(sketch, "E10.0.1.101", {"start": v(1.39, 6.27) * mm, "end": v(2.86, 6.27) * mm});
            skLineSegment(sketch, "E10.0.1.102", {"start": v(9.89, 6.27) * mm, "end": v(11.36, 6.27) * mm});
            skLineSegment(sketch, "E10.0.1.103", {"start": v(8.85, -6.99) * mm, "end": v(8.85, -5.51) * mm});
            skLineSegment(sketch, "E10.0.1.104", {"start": v(8.15, -5.51) * mm, "end": v(8.15, -6.99) * mm});
            skLineSegment(sketch, "E10.0.1.105", {"start": v(9.89, -4.48) * mm, "end": v(11.36, -4.48) * mm});
            skLineSegment(sketch, "E10.0.1.106", {"start": v(11.36, -8.03) * mm, "end": v(9.89, -8.03) * mm});
            skLineSegment(sketch, "E10.0.1.107", {"start": v(5.64, -4.48) * mm, "end": v(7.11, -4.48) * mm});
            skLineSegment(sketch, "E10.0.1.108", {"start": v(14.14, -8.03) * mm, "end": v(13.1, -6.99) * mm});
            skLineSegment(sketch, "E10.0.1.109", {"start": v(2.86, -4.47) * mm, "end": v(3.9, -5.51) * mm});
            skLineSegment(sketch, "E10.0.1.110", {"start": v(7.11, -8.03) * mm, "end": v(5.64, -8.03) * mm});
            skLineSegment(sketch, "E10.0.1.111", {"start": v(15.61, -8.03) * mm, "end": v(14.14, -8.03) * mm});
            skLineSegment(sketch, "E10.0.1.112", {"start": v(-4.6, -5.51) * mm, "end": v(-4.6, -6.99) * mm});
            skLineSegment(sketch, "E10.0.1.113", {"start": v(-14.14, -8.03) * mm, "end": v(-15.61, -8.03) * mm});
            skLineSegment(sketch, "E10.0.1.114", {"start": v(4.6, 5.24) * mm, "end": v(5.64, 6.27) * mm});
            skLineSegment(sketch, "E10.0.1.115", {"start": v(4.6, -5.51) * mm, "end": v(5.64, -4.48) * mm});
            skLineSegment(sketch, "E10.0.1.116", {"start": v(-11.36, 2.72) * mm, "end": v(-12.4, 3.76) * mm});
            skLineSegment(sketch, "E10.0.1.117", {"start": v(-2.86, 2.72) * mm, "end": v(-3.9, 3.76) * mm});
            skLineSegment(sketch, "E10.0.1.118", {"start": v(-15.61, 2.72) * mm, "end": v(-16.65, 3.76) * mm});
            skLineSegment(sketch, "E10.0.1.119", {"start": v(-11.36, -8.03) * mm, "end": v(-12.4, -6.99) * mm});
            skLineSegment(sketch, "E10.0.1.120", {"start": v(-2.86, -8.03) * mm, "end": v(-3.9, -6.99) * mm});
            skLineSegment(sketch, "E10.0.1.121", {"start": v(-15.61, -8.03) * mm, "end": v(-16.65, -6.99) * mm});
            skLineSegment(sketch, "E10.0.1.122", {"start": v(13.1, -5.51) * mm, "end": v(14.14, -4.48) * mm});
            skLineSegment(sketch, "E10.0.1.123", {"start": v(-2.86, -4.48) * mm, "end": v(-1.39, -4.48) * mm});
            skLineSegment(sketch, "E10.0.1.124", {"start": v(-16.65, 3.76) * mm, "end": v(-16.65, 5.24) * mm});
            skLineSegment(sketch, "E10.0.1.125", {"start": v(8.85, -5.51) * mm, "end": v(9.89, -4.48) * mm});
            skLineSegment(sketch, "E10.0.1.126", {"start": v(3.9, 5.24) * mm, "end": v(3.9, 3.76) * mm});
            skLineSegment(sketch, "E10.0.1.127", {"start": v(3.9, -5.51) * mm, "end": v(3.9, -6.99) * mm});
            skLineSegment(sketch, "E10.0.1.128", {"start": v(-14.14, 6.28) * mm, "end": v(-13.1, 5.24) * mm});
            skLineSegment(sketch, "E10.0.1.129", {"start": v(-14.14, -4.47) * mm, "end": v(-13.1, -5.51) * mm});
            skLineSegment(sketch, "E10.direction1", {"start": v(-15.61, -12.28) * mm, "end": v(9.39, -12.28) * mm, "construction": true});
            skLineSegment(sketch, "E10.direction2", {"start": v(-15.61, -12.28) * mm, "end": v(-15.61, -8.03) * mm, "construction": true});
            skLineSegment(sketch, "E11.bottom", {"start": v(23, -13.75) * mm, "end": v(-23, -13.75) * mm});
            skLineSegment(sketch, "E11.top", {"start": v(23, 14.25) * mm, "end": v(-23, 14.25) * mm});
            skLineSegment(sketch, "E11.left", {"start": v(32, -3.5) * mm, "end": v(32, 3.5) * mm});
            skLineSegment(sketch, "E11.right", {"start": v(-32, -3.5) * mm, "end": v(-32, 3.5) * mm});
            skPoint(sketch, "E11.middle", {"position": v(0, 0.25) * mm});
            skPoint(sketch, "E11.middle.positionSnap0", {"position": v(0.35, 0.25) * mm});
            skPoint(sketch, "E11.centerSnap0", {"position": v(0.35, 0.25) * mm});
            skLineSegment(sketch, "E12", {"start": v(-32, 3.5) * mm, "end": v(-23, 3.5) * mm});
            skLineSegment(sketch, "E13", {"start": v(-23, 3.5) * mm, "end": v(-23, 14.25) * mm});
            skLineSegment(sketch, "E14.MirrorCS", {"start": v(23, 3.5) * mm, "end": v(23, 14.25) * mm});
            skLineSegment(sketch, "E15.MirrorCS", {"start": v(32, 3.5) * mm, "end": v(23, 3.5) * mm});
            skLineSegment(sketch, "E16.MirrorCS", {"start": v(32, -3.5) * mm, "end": v(23, -3.5) * mm});
            skLineSegment(sketch, "E17.MirrorCS", {"start": v(23, -3.5) * mm, "end": v(23, -13.75) * mm});
            skLineSegment(sketch, "E18.MirrorCS", {"start": v(-32, -3.5) * mm, "end": v(-23, -3.5) * mm});
            skLineSegment(sketch, "E19.MirrorCS", {"start": v(-23, -3.5) * mm, "end": v(-23, -13.75) * mm});
            skPoint(sketch, "E20.orphan", {"position": v(-32, -13.75) * mm});
            skPoint(sketch, "E21.orphan", {"position": v(-32, 14.25) * mm});
            skPoint(sketch, "E22.orphan", {"position": v(32, 14.25) * mm});
            skPoint(sketch, "E23.orphan", {"position": v(32, -13.75) * mm});
            skPoint(sketch, "E24.orphan", {"position": v(23, -14.25) * mm});
            skPoint(sketch, "E25.orphan", {"position": v(-23, -14.25) * mm});
            skSolve(sketch);
        }
        {
            var Q0;
            Q0=qCreatedBy(makeId("Top.planeOp"),FACE);
            var sketch = newSketch(context, id + "F1", { "sketchPlane" : qUnion([Q0])});
            skLineSegment(sketch, "E26.bottom", {"start": v(-2.38, 10.5) * mm, "end": v(-14.38, 10.5) * mm});
            skLineSegment(sketch, "E26.top", {"start": v(-2.38, 11.5) * mm, "end": v(-14.38, 11.5) * mm});
            skLineSegment(sketch, "E26.left", {"start": v(-2.38, 10.5) * mm, "end": v(-2.38, 11.5) * mm});
            skLineSegment(sketch, "E26.right", {"start": v(-14.38, 10.5) * mm, "end": v(-14.38, 11.5) * mm});
            skPoint(sketch, "E26.middle", {"position": v(-8.38, 11) * mm});
            skLineSegment(sketch, "E27.bottom", {"start": v(-2.38, 5) * mm, "end": v(-14.38, 5) * mm});
            skLineSegment(sketch, "E27.top", {"start": v(-2.38, 4) * mm, "end": v(-14.38, 4) * mm});
            skLineSegment(sketch, "E27.left", {"start": v(-2.38, 5) * mm, "end": v(-2.38, 4) * mm});
            skLineSegment(sketch, "E27.right", {"start": v(-14.38, 5) * mm, "end": v(-14.38, 4) * mm});
            skPoint(sketch, "E27.middle", {"position": v(-8.38, 4.5) * mm});
            skLineSegment(sketch, "E28.bottom", {"start": v(-2.38, 0.75) * mm, "end": v(-14.37, 0.75) * mm});
            skLineSegment(sketch, "E28.top", {"start": v(-2.38, -0.25) * mm, "end": v(-14.37, -0.25) * mm});
            skLineSegment(sketch, "E28.left", {"start": v(-2.38, 0.75) * mm, "end": v(-2.38, -0.25) * mm});
            skLineSegment(sketch, "E28.right", {"start": v(-14.38, 0.75) * mm, "end": v(-14.38, -0.25) * mm});
            skPoint(sketch, "E28.middle", {"position": v(-8.38, 0.25) * mm});
            skLineSegment(sketch, "E29.bottom", {"start": v(-2.38, -5.75) * mm, "end": v(-14.37, -5.75) * mm});
            skLineSegment(sketch, "E29.top", {"start": v(-2.38, -6.75) * mm, "end": v(-14.38, -6.75) * mm});
            skLineSegment(sketch, "E29.left", {"start": v(-2.38, -5.75) * mm, "end": v(-2.38, -6.75) * mm});
            skLineSegment(sketch, "E29.right", {"start": v(-14.38, -5.75) * mm, "end": v(-14.38, -6.75) * mm});
            skPoint(sketch, "E29.middle", {"position": v(-8.38, -6.25) * mm});
            skLineSegment(sketch, "E30.bottom", {"start": v(-2.38, -10) * mm, "end": v(-14.38, -10) * mm});
            skLineSegment(sketch, "E30.top", {"start": v(-2.38, -11) * mm, "end": v(-14.37, -11) * mm});
            skLineSegment(sketch, "E30.left", {"start": v(-2.38, -10) * mm, "end": v(-2.38, -11) * mm});
            skLineSegment(sketch, "E30.right", {"start": v(-14.38, -10) * mm, "end": v(-14.38, -11) * mm});
            skPoint(sketch, "E30.middle", {"position": v(-8.38, -10.5) * mm});
            skLineSegment(sketch, "E31.MirrorCS", {"start": v(14.38, -10) * mm, "end": v(14.38, -11) * mm});
            skLineSegment(sketch, "E32.MirrorCS", {"start": v(2.38, 0.75) * mm, "end": v(2.38, -0.25) * mm});
            skLineSegment(sketch, "E33.MirrorCS", {"start": v(14.38, 0.75) * mm, "end": v(14.38, -0.25) * mm});
            skLineSegment(sketch, "E34.MirrorCS", {"start": v(2.38, -10) * mm, "end": v(2.38, -11) * mm});
            skLineSegment(sketch, "E35.MirrorCS", {"start": v(2.38, -5.75) * mm, "end": v(2.38, -6.75) * mm});
            skLineSegment(sketch, "E36.MirrorCS", {"start": v(14.38, -5.75) * mm, "end": v(14.38, -6.75) * mm});
            skLineSegment(sketch, "E37.MirrorCS", {"start": v(2.38, 10.5) * mm, "end": v(2.38, 11.5) * mm});
            skLineSegment(sketch, "E38.MirrorCS", {"start": v(2.38, 5) * mm, "end": v(2.38, 4) * mm});
            skLineSegment(sketch, "E39.MirrorCS", {"start": v(14.38, 10.5) * mm, "end": v(14.38, 11.5) * mm});
            skLineSegment(sketch, "E40.MirrorCS", {"start": v(14.38, 5) * mm, "end": v(14.38, 4) * mm});
            skPoint(sketch, "E41.MirrorP", {"position": v(8.38, 0.25) * mm});
            skLineSegment(sketch, "E42.MirrorCS", {"start": v(2.38, -0.25) * mm, "end": v(14.37, -0.25) * mm});
            skLineSegment(sketch, "E43.MirrorCS", {"start": v(2.38, -10) * mm, "end": v(14.38, -10) * mm});
            skLineSegment(sketch, "E44.MirrorCS", {"start": v(2.38, -5.75) * mm, "end": v(14.37, -5.75) * mm});
            skPoint(sketch, "E45.MirrorP", {"position": v(8.38, 4.5) * mm});
            skPoint(sketch, "E46.MirrorP", {"position": v(8.38, -6.25) * mm});
            skPoint(sketch, "E47.MirrorP", {"position": v(8.38, -10.5) * mm});
            skLineSegment(sketch, "E48.MirrorCS", {"start": v(2.38, -6.75) * mm, "end": v(14.38, -6.75) * mm});
            skPoint(sketch, "E49.MirrorP", {"position": v(8.38, 11) * mm});
            skLineSegment(sketch, "E50.MirrorCS", {"start": v(2.38, -11) * mm, "end": v(14.37, -11) * mm});
            skLineSegment(sketch, "E51.MirrorCS", {"start": v(2.38, 10.5) * mm, "end": v(14.38, 10.5) * mm});
            skLineSegment(sketch, "E52.MirrorCS", {"start": v(2.38, 11.5) * mm, "end": v(14.38, 11.5) * mm});
            skLineSegment(sketch, "E53.MirrorCS", {"start": v(2.38, 4) * mm, "end": v(14.38, 4) * mm});
            skLineSegment(sketch, "E54.MirrorCS", {"start": v(2.38, 0.75) * mm, "end": v(14.37, 0.75) * mm});
            skLineSegment(sketch, "E55.MirrorCS", {"start": v(2.38, 5) * mm, "end": v(14.38, 5) * mm});
            skSolve(sketch);
        }
        {
            var Q0;
            Q0=qCreatedBy(makeId("Top.planeOp"),FACE);
            var sketch = newSketch(context, id + "F2", { "sketchPlane" : qUnion([Q0])});
            skCircle(sketch, "E56.cCircle", {"center": v(-14.88, 11) * mm, "radius": 1.8 * mm, "construction": true});
            skLineSegment(sketch, "E56.0", {"start": v(-15.91, 12.8) * mm, "end": v(-13.84, 12.8) * mm});
            skLineSegment(sketch, "E56.1", {"start": v(-13.84, 12.8) * mm, "end": v(-13.23, 11.75) * mm});
            skLineSegment(sketch, "E56.2", {"start": v(-13.23, 10.25) * mm, "end": v(-13.84, 9.2) * mm});
            skLineSegment(sketch, "E56.3", {"start": v(-13.84, 9.2) * mm, "end": v(-15.91, 9.2) * mm});
            skLineSegment(sketch, "E56.4", {"start": v(-15.91, 9.2) * mm, "end": v(-16.16, 9.62) * mm});
            skLineSegment(sketch, "E56.5", {"start": v(-16.88, 11.12) * mm, "end": v(-15.91, 12.8) * mm});
            skPoint(sketch, "E56.0.midPoint", {"position": v(-14.88, 12.8) * mm});
            skLineSegment(sketch, "E57.1.0.0", {"start": v(-9.59, 9.2) * mm, "end": v(-11.66, 9.2) * mm});
            skLineSegment(sketch, "E57.1.0.1", {"start": v(-8.98, 10.25) * mm, "end": v(-9.59, 9.2) * mm});
            skLineSegment(sketch, "E57.1.0.2", {"start": v(-9.59, 12.8) * mm, "end": v(-8.98, 11.75) * mm});
            skLineSegment(sketch, "E57.1.0.3", {"start": v(-11.66, 12.8) * mm, "end": v(-9.59, 12.8) * mm});
            skLineSegment(sketch, "E57.1.0.4", {"start": v(-12.27, 11.75) * mm, "end": v(-11.66, 12.8) * mm});
            skLineSegment(sketch, "E57.1.0.5", {"start": v(-11.66, 9.2) * mm, "end": v(-12.27, 10.25) * mm});
            skLineSegment(sketch, "E57.2.0.0", {"start": v(-5.34, 9.2) * mm, "end": v(-7.41, 9.2) * mm});
            skLineSegment(sketch, "E57.2.0.1", {"start": v(-4.73, 10.25) * mm, "end": v(-5.34, 9.2) * mm});
            skLineSegment(sketch, "E57.2.0.2", {"start": v(-5.34, 12.8) * mm, "end": v(-4.73, 11.75) * mm});
            skLineSegment(sketch, "E57.2.0.3", {"start": v(-7.41, 12.8) * mm, "end": v(-5.34, 12.8) * mm});
            skLineSegment(sketch, "E57.2.0.4", {"start": v(-8.02, 11.75) * mm, "end": v(-7.41, 12.8) * mm});
            skLineSegment(sketch, "E57.2.0.5", {"start": v(-7.41, 9.2) * mm, "end": v(-8.02, 10.25) * mm});
            skLineSegment(sketch, "E57.3.0.0", {"start": v(-1.09, 9.2) * mm, "end": v(-3.16, 9.2) * mm});
            skLineSegment(sketch, "E57.3.0.1", {"start": v(-0.48, 10.25) * mm, "end": v(-1.09, 9.2) * mm});
            skLineSegment(sketch, "E57.3.0.2", {"start": v(-1.09, 12.8) * mm, "end": v(-0.48, 11.75) * mm});
            skLineSegment(sketch, "E57.3.0.3", {"start": v(-3.16, 12.8) * mm, "end": v(-1.09, 12.8) * mm});
            skLineSegment(sketch, "E57.3.0.4", {"start": v(-3.77, 11.75) * mm, "end": v(-3.16, 12.8) * mm});
            skLineSegment(sketch, "E57.3.0.5", {"start": v(-3.16, 9.2) * mm, "end": v(-3.77, 10.25) * mm});
            skLineSegment(sketch, "E57.4.0.0", {"start": v(3.16, 9.2) * mm, "end": v(1.09, 9.2) * mm});
            skLineSegment(sketch, "E57.4.0.1", {"start": v(3.77, 10.25) * mm, "end": v(3.16, 9.2) * mm});
            skLineSegment(sketch, "E57.4.0.2", {"start": v(3.16, 12.8) * mm, "end": v(3.77, 11.75) * mm});
            skLineSegment(sketch, "E57.4.0.3", {"start": v(1.09, 12.8) * mm, "end": v(3.16, 12.8) * mm});
            skLineSegment(sketch, "E57.4.0.4", {"start": v(0.48, 11.75) * mm, "end": v(1.09, 12.8) * mm});
            skLineSegment(sketch, "E57.4.0.5", {"start": v(1.09, 9.2) * mm, "end": v(0.48, 10.25) * mm});
            skLineSegment(sketch, "E57.5.0.0", {"start": v(7.41, 9.2) * mm, "end": v(5.34, 9.2) * mm});
            skLineSegment(sketch, "E57.5.0.1", {"start": v(8.02, 10.25) * mm, "end": v(7.41, 9.2) * mm});
            skLineSegment(sketch, "E57.5.0.2", {"start": v(7.41, 12.8) * mm, "end": v(8.02, 11.75) * mm});
            skLineSegment(sketch, "E57.5.0.3", {"start": v(5.34, 12.8) * mm, "end": v(7.41, 12.8) * mm});
            skLineSegment(sketch, "E57.5.0.4", {"start": v(4.73, 11.75) * mm, "end": v(5.34, 12.8) * mm});
            skLineSegment(sketch, "E57.5.0.5", {"start": v(5.34, 9.2) * mm, "end": v(4.73, 10.25) * mm});
            skLineSegment(sketch, "E57.6.0.0", {"start": v(11.66, 9.2) * mm, "end": v(9.59, 9.2) * mm});
            skLineSegment(sketch, "E57.6.0.1", {"start": v(12.27, 10.25) * mm, "end": v(11.66, 9.2) * mm});
            skLineSegment(sketch, "E57.6.0.2", {"start": v(11.66, 12.8) * mm, "end": v(12.27, 11.75) * mm});
            skLineSegment(sketch, "E57.6.0.3", {"start": v(9.59, 12.8) * mm, "end": v(11.66, 12.8) * mm});
            skLineSegment(sketch, "E57.6.0.4", {"start": v(8.98, 11.75) * mm, "end": v(9.59, 12.8) * mm});
            skLineSegment(sketch, "E57.6.0.5", {"start": v(9.59, 9.2) * mm, "end": v(8.98, 10.25) * mm});
            skLineSegment(sketch, "E57.7.0.0", {"start": v(15.91, 9.2) * mm, "end": v(13.84, 9.2) * mm});
            skLineSegment(sketch, "E57.7.0.1", {"start": v(16.16, 9.62) * mm, "end": v(15.91, 9.2) * mm});
            skLineSegment(sketch, "E57.7.0.2", {"start": v(15.91, 12.8) * mm, "end": v(16.88, 11.12) * mm});
            skLineSegment(sketch, "E57.7.0.3", {"start": v(13.84, 12.8) * mm, "end": v(15.91, 12.8) * mm});
            skLineSegment(sketch, "E57.7.0.4", {"start": v(13.23, 11.75) * mm, "end": v(13.84, 12.8) * mm});
            skLineSegment(sketch, "E57.7.0.5", {"start": v(13.84, 9.2) * mm, "end": v(13.23, 10.25) * mm});
            skLineSegment(sketch, "E57.direction1", {"start": v(-15.91, 9.2) * mm, "end": v(-11.66, 9.2) * mm, "construction": true});
            skLineSegment(sketch, "E58.bottom", {"start": v(13.23, 10.25) * mm, "end": v(12.27, 10.25) * mm});
            skLineSegment(sketch, "E58.top", {"start": v(13.23, 11.75) * mm, "end": v(12.27, 11.75) * mm});
            skPoint(sketch, "E58.middle", {"position": v(0.05, 11) * mm});
            skPoint(sketch, "E59.orphan", {"position": v(-14.95, 10.25) * mm});
            skPoint(sketch, "E60.orphan", {"position": v(-14.95, 11.75) * mm});
            skPoint(sketch, "E61.orphan", {"position": v(-12.8, 11) * mm});
            skPoint(sketch, "E62.orphan", {"position": v(-12.7, 11) * mm});
            skPoint(sketch, "E63.orphan", {"position": v(-4.3, 11) * mm});
            skPoint(sketch, "E64.orphan", {"position": v(-8.45, 11) * mm});
            skPoint(sketch, "E65.orphan", {"position": v(-8.55, 11) * mm});
            skPoint(sketch, "E66.orphan", {"position": v(-4.2, 11) * mm});
            skPoint(sketch, "E67.orphan", {"position": v(-0.05, 11) * mm});
            skPoint(sketch, "E68.orphan", {"position": v(4.2, 11) * mm});
            skPoint(sketch, "E69.orphan", {"position": v(4.3, 11) * mm});
            skPoint(sketch, "E70.orphan", {"position": v(8.45, 11) * mm});
            skPoint(sketch, "E71.orphan", {"position": v(8.55, 11) * mm});
            skPoint(sketch, "E72.orphan", {"position": v(12.7, 11) * mm});
            skPoint(sketch, "E73.orphan", {"position": v(12.8, 11) * mm});
            skPoint(sketch, "E58.left.end.orphan", {"position": v(15.05, 11.75) * mm});
            skPoint(sketch, "E58.left.start.orphan", {"position": v(15.05, 10.25) * mm});
            skLineSegment(sketch, "E74.trimOffspring", {"start": v(-12.27, 11.75) * mm, "end": v(-13.24, 11.75) * mm});
            skLineSegment(sketch, "E75.trimOffspring", {"start": v(-12.27, 10.25) * mm, "end": v(-13.24, 10.25) * mm});
            skLineSegment(sketch, "E76.trimOffspring", {"start": v(-8.02, 11.75) * mm, "end": v(-8.98, 11.75) * mm});
            skLineSegment(sketch, "E77.trimOffspring", {"start": v(-8.02, 10.25) * mm, "end": v(-8.98, 10.25) * mm});
            skLineSegment(sketch, "E78.trimOffspring", {"start": v(-3.77, 11.75) * mm, "end": v(-4.73, 11.75) * mm});
            skLineSegment(sketch, "E79.trimOffspring", {"start": v(-3.77, 10.25) * mm, "end": v(-4.73, 10.25) * mm});
            skLineSegment(sketch, "E80.trimOffspring", {"start": v(0.48, 11.75) * mm, "end": v(-0.48, 11.75) * mm});
            skLineSegment(sketch, "E81.trimOffspring", {"start": v(0.48, 10.25) * mm, "end": v(-0.48, 10.25) * mm});
            skLineSegment(sketch, "E82.trimOffspring", {"start": v(4.73, 11.75) * mm, "end": v(3.77, 11.75) * mm});
            skLineSegment(sketch, "E83.trimOffspring", {"start": v(4.73, 10.25) * mm, "end": v(3.77, 10.25) * mm});
            skLineSegment(sketch, "E84.trimOffspring", {"start": v(8.98, 11.75) * mm, "end": v(8.02, 11.75) * mm});
            skLineSegment(sketch, "E85.trimOffspring", {"start": v(8.98, 10.25) * mm, "end": v(8.02, 10.25) * mm});
            skLineSegment(sketch, "E86.0.1.0", {"start": v(1.09, 2.05) * mm, "end": v(3.16, 2.05) * mm});
            skPoint(sketch, "E86.0.1.1", {"position": v(0.05, 0.25) * mm});
            skPoint(sketch, "E86.0.1.2", {"position": v(15.05, -0.5) * mm});
            skPoint(sketch, "E86.0.1.3", {"position": v(-14.95, -0.5) * mm});
            skLineSegment(sketch, "E86.0.1.4", {"start": v(3.16, -1.55) * mm, "end": v(1.09, -1.55) * mm});
            skPoint(sketch, "E86.0.1.5", {"position": v(-0.02, 0.4) * mm});
            skLineSegment(sketch, "E86.0.1.6", {"start": v(-1.09, -1.55) * mm, "end": v(-3.16, -1.55) * mm});
            skPoint(sketch, "E86.0.1.7", {"position": v(15.05, 1) * mm});
            skCircle(sketch, "E86.0.1.8", {"center": v(-14.88, 0.25) * mm, "radius": 1.8 * mm, "construction": true});
            skPoint(sketch, "E86.0.1.9", {"position": v(-4.3, 0.25) * mm});
            skLineSegment(sketch, "E86.0.1.10", {"start": v(-9.59, -1.55) * mm, "end": v(-11.66, -1.55) * mm});
            skLineSegment(sketch, "E86.0.1.11", {"start": v(7.41, -1.55) * mm, "end": v(5.34, -1.55) * mm});
            skLineSegment(sketch, "E86.0.1.12", {"start": v(-3.16, 2.05) * mm, "end": v(-1.09, 2.05) * mm});
            skPoint(sketch, "E86.0.1.13", {"position": v(-8.45, 0.25) * mm});
            skPoint(sketch, "E86.0.1.14", {"position": v(12.8, 0.25) * mm});
            skPoint(sketch, "E86.0.1.15", {"position": v(-12.7, 0.25) * mm});
            skLineSegment(sketch, "E86.0.1.16", {"start": v(11.66, -1.55) * mm, "end": v(9.59, -1.55) * mm});
            skLineSegment(sketch, "E86.0.1.17", {"start": v(15.91, -1.55) * mm, "end": v(13.84, -1.55) * mm});
            skLineSegment(sketch, "E86.0.1.18", {"start": v(13.84, 2.05) * mm, "end": v(15.91, 2.05) * mm});
            skLineSegment(sketch, "E86.0.1.19", {"start": v(16.95, 0.25) * mm, "end": v(15.91, -1.55) * mm});
            skLineSegment(sketch, "E86.0.1.20", {"start": v(15.91, 2.05) * mm, "end": v(16.95, 0.25) * mm});
            skPoint(sketch, "E86.0.1.21", {"position": v(4.3, 0.25) * mm});
            skLineSegment(sketch, "E86.0.1.22", {"start": v(9.59, 2.05) * mm, "end": v(11.66, 2.05) * mm});
            skLineSegment(sketch, "E86.0.1.23", {"start": v(-5.34, -1.55) * mm, "end": v(-7.41, -1.55) * mm});
            skPoint(sketch, "E86.0.1.24", {"position": v(-14.88, 2.05) * mm});
            skLineSegment(sketch, "E86.0.1.25", {"start": v(-11.66, 2.05) * mm, "end": v(-9.59, 2.05) * mm});
            skLineSegment(sketch, "E86.0.1.26", {"start": v(5.34, 2.05) * mm, "end": v(7.41, 2.05) * mm});
            skPoint(sketch, "E86.0.1.27", {"position": v(-4.2, 0.25) * mm});
            skLineSegment(sketch, "E86.0.1.28", {"start": v(-7.41, 2.05) * mm, "end": v(-5.34, 2.05) * mm});
            skPoint(sketch, "E86.0.1.30", {"position": v(8.45, 0.25) * mm});
            skLineSegment(sketch, "E86.0.1.31", {"start": v(-16.95, 0.25) * mm, "end": v(-15.91, 2.05) * mm});
            skPoint(sketch, "E86.0.1.32", {"position": v(4.2, 0.25) * mm});
            skPoint(sketch, "E86.0.1.33", {"position": v(-12.8, 0.25) * mm});
            skLineSegment(sketch, "E86.0.1.34", {"start": v(-15.91, -1.55) * mm, "end": v(-16.95, 0.25) * mm});
            skPoint(sketch, "E86.0.1.35", {"position": v(12.7, 0.25) * mm});
            skPoint(sketch, "E86.0.1.36", {"position": v(-8.55, 0.25) * mm});
            skPoint(sketch, "E86.0.1.37", {"position": v(8.55, 0.25) * mm});
            skPoint(sketch, "E86.0.1.38", {"position": v(-14.95, 1) * mm});
            skLineSegment(sketch, "E86.0.1.39", {"start": v(-15.91, 2.05) * mm, "end": v(-13.84, 2.05) * mm});
            skLineSegment(sketch, "E86.0.1.40", {"start": v(-13.84, -1.55) * mm, "end": v(-15.91, -1.55) * mm});
            skLineSegment(sketch, "E86.0.1.41", {"start": v(-13.84, 2.05) * mm, "end": v(-13.23, 1) * mm});
            skLineSegment(sketch, "E86.0.1.42", {"start": v(12.27, -0.5) * mm, "end": v(11.66, -1.55) * mm});
            skLineSegment(sketch, "E86.0.1.43", {"start": v(-3.77, -0.5) * mm, "end": v(-4.73, -0.5) * mm});
            skLineSegment(sketch, "E86.0.1.44", {"start": v(-12.27, -0.5) * mm, "end": v(-13.24, -0.5) * mm});
            skLineSegment(sketch, "E86.0.1.45", {"start": v(7.41, 2.05) * mm, "end": v(8.02, 1) * mm});
            skLineSegment(sketch, "E86.0.1.46", {"start": v(-8.02, 1) * mm, "end": v(-7.41, 2.05) * mm});
            skLineSegment(sketch, "E86.0.1.47", {"start": v(-3.77, 1) * mm, "end": v(-3.16, 2.05) * mm});
            skLineSegment(sketch, "E86.0.1.48", {"start": v(13.23, 1) * mm, "end": v(12.27, 1) * mm});
            skLineSegment(sketch, "E86.0.1.49", {"start": v(0.48, 1) * mm, "end": v(-0.48, 1) * mm});
            skLineSegment(sketch, "E86.0.1.50", {"start": v(4.73, 1) * mm, "end": v(5.34, 2.05) * mm});
            skLineSegment(sketch, "E86.0.1.51", {"start": v(3.77, -0.5) * mm, "end": v(3.16, -1.55) * mm});
            skLineSegment(sketch, "E86.0.1.52", {"start": v(13.23, -0.5) * mm, "end": v(12.27, -0.5) * mm});
            skLineSegment(sketch, "E86.0.1.53", {"start": v(9.59, -1.55) * mm, "end": v(8.98, -0.5) * mm});
            skLineSegment(sketch, "E86.0.1.54", {"start": v(13.23, 1) * mm, "end": v(13.84, 2.05) * mm});
            skLineSegment(sketch, "E86.0.1.55", {"start": v(-8.02, 1) * mm, "end": v(-8.98, 1) * mm});
            skLineSegment(sketch, "E86.0.1.56", {"start": v(8.02, -0.5) * mm, "end": v(7.41, -1.55) * mm});
            skLineSegment(sketch, "E86.0.1.57", {"start": v(1.09, -1.55) * mm, "end": v(0.48, -0.5) * mm});
            skLineSegment(sketch, "E86.0.1.58", {"start": v(-11.66, -1.55) * mm, "end": v(-12.27, -0.5) * mm});
            skLineSegment(sketch, "E86.0.1.59", {"start": v(11.66, 2.05) * mm, "end": v(12.27, 1) * mm});
            skLineSegment(sketch, "E86.0.1.60", {"start": v(-8.02, -0.5) * mm, "end": v(-8.98, -0.5) * mm});
            skLineSegment(sketch, "E86.0.1.61", {"start": v(0.48, -0.5) * mm, "end": v(-0.48, -0.5) * mm});
            skLineSegment(sketch, "E86.0.1.62", {"start": v(3.16, 2.05) * mm, "end": v(3.77, 1) * mm});
            skLineSegment(sketch, "E86.0.1.63", {"start": v(0.48, 1) * mm, "end": v(1.09, 2.05) * mm});
            skLineSegment(sketch, "E86.0.1.64", {"start": v(-12.27, 1) * mm, "end": v(-11.66, 2.05) * mm});
            skLineSegment(sketch, "E86.0.1.65", {"start": v(4.73, 1) * mm, "end": v(3.77, 1) * mm});
            skLineSegment(sketch, "E86.0.1.66", {"start": v(13.84, -1.55) * mm, "end": v(13.23, -0.5) * mm});
            skLineSegment(sketch, "E86.0.1.67", {"start": v(-5.34, 2.05) * mm, "end": v(-4.73, 1) * mm});
            skLineSegment(sketch, "E86.0.1.68", {"start": v(-3.77, 1) * mm, "end": v(-4.73, 1) * mm});
            skLineSegment(sketch, "E86.0.1.69", {"start": v(-0.48, -0.5) * mm, "end": v(-1.09, -1.55) * mm});
            skLineSegment(sketch, "E86.0.1.70", {"start": v(8.98, 1) * mm, "end": v(9.59, 2.05) * mm});
            skLineSegment(sketch, "E86.0.1.71", {"start": v(5.34, -1.55) * mm, "end": v(4.73, -0.5) * mm});
            skLineSegment(sketch, "E86.0.1.72", {"start": v(-3.16, -1.55) * mm, "end": v(-3.77, -0.5) * mm});
            skLineSegment(sketch, "E86.0.1.73", {"start": v(-1.09, 2.05) * mm, "end": v(-0.48, 1) * mm});
            skLineSegment(sketch, "E86.0.1.74", {"start": v(4.73, -0.5) * mm, "end": v(3.77, -0.5) * mm});
            skLineSegment(sketch, "E86.0.1.75", {"start": v(-12.27, 1) * mm, "end": v(-13.24, 1) * mm});
            skLineSegment(sketch, "E86.0.1.76", {"start": v(-8.98, -0.5) * mm, "end": v(-9.59, -1.55) * mm});
            skLineSegment(sketch, "E86.0.1.77", {"start": v(-9.59, 2.05) * mm, "end": v(-8.98, 1) * mm});
            skLineSegment(sketch, "E86.0.1.78", {"start": v(8.98, -0.5) * mm, "end": v(8.02, -0.5) * mm});
            skLineSegment(sketch, "E86.0.1.79", {"start": v(-7.41, -1.55) * mm, "end": v(-8.02, -0.5) * mm});
            skLineSegment(sketch, "E86.0.1.80", {"start": v(-4.73, -0.5) * mm, "end": v(-5.34, -1.55) * mm});
            skLineSegment(sketch, "E86.0.1.81", {"start": v(-13.23, -0.5) * mm, "end": v(-13.84, -1.55) * mm});
            skLineSegment(sketch, "E86.0.1.82", {"start": v(8.98, 1) * mm, "end": v(8.02, 1) * mm});
            skLineSegment(sketch, "E86.0.2.0", {"start": v(1.09, -8.7) * mm, "end": v(3.16, -8.7) * mm});
            skPoint(sketch, "E86.0.2.1", {"position": v(0.05, -10.5) * mm});
            skPoint(sketch, "E86.0.2.2", {"position": v(15.05, -11.25) * mm});
            skPoint(sketch, "E86.0.2.3", {"position": v(-14.95, -11.25) * mm});
            skLineSegment(sketch, "E86.0.2.4", {"start": v(3.16, -12.3) * mm, "end": v(1.09, -12.3) * mm});
            skPoint(sketch, "E86.0.2.5", {"position": v(-0.05, -10.5) * mm});
            skLineSegment(sketch, "E86.0.2.6", {"start": v(-1.09, -12.3) * mm, "end": v(-3.16, -12.3) * mm});
            skPoint(sketch, "E86.0.2.7", {"position": v(15.05, -9.75) * mm});
            skCircle(sketch, "E86.0.2.8", {"center": v(-14.88, -10.5) * mm, "radius": 1.8 * mm, "construction": true});
            skPoint(sketch, "E86.0.2.9", {"position": v(-4.3, -10.5) * mm});
            skLineSegment(sketch, "E86.0.2.10", {"start": v(-9.59, -12.3) * mm, "end": v(-11.66, -12.3) * mm});
            skLineSegment(sketch, "E86.0.2.11", {"start": v(7.41, -12.3) * mm, "end": v(5.34, -12.3) * mm});
            skLineSegment(sketch, "E86.0.2.12", {"start": v(-3.16, -8.7) * mm, "end": v(-1.09, -8.7) * mm});
            skPoint(sketch, "E86.0.2.13", {"position": v(-8.45, -10.5) * mm});
            skPoint(sketch, "E86.0.2.14", {"position": v(12.8, -10.5) * mm});
            skPoint(sketch, "E86.0.2.15", {"position": v(-12.7, -10.5) * mm});
            skLineSegment(sketch, "E86.0.2.16", {"start": v(11.66, -12.3) * mm, "end": v(9.59, -12.3) * mm});
            skLineSegment(sketch, "E86.0.2.17", {"start": v(15.91, -12.3) * mm, "end": v(13.84, -12.3) * mm});
            skLineSegment(sketch, "E86.0.2.18", {"start": v(13.84, -8.7) * mm, "end": v(15.91, -8.7) * mm});
            skLineSegment(sketch, "E86.0.2.19", {"start": v(16.6, -11.13) * mm, "end": v(15.91, -12.3) * mm});
            skLineSegment(sketch, "E86.0.2.20", {"start": v(15.91, -8.7) * mm, "end": v(16.45, -9.62) * mm});
            skPoint(sketch, "E86.0.2.21", {"position": v(4.3, -10.5) * mm});
            skLineSegment(sketch, "E86.0.2.22", {"start": v(9.59, -8.7) * mm, "end": v(11.66, -8.7) * mm});
            skLineSegment(sketch, "E86.0.2.23", {"start": v(-5.34, -12.3) * mm, "end": v(-7.41, -12.3) * mm});
            skPoint(sketch, "E86.0.2.24", {"position": v(-14.88, -8.7) * mm});
            skLineSegment(sketch, "E86.0.2.25", {"start": v(-11.66, -8.7) * mm, "end": v(-9.59, -8.7) * mm});
            skLineSegment(sketch, "E86.0.2.26", {"start": v(5.34, -8.7) * mm, "end": v(7.41, -8.7) * mm});
            skPoint(sketch, "E86.0.2.27", {"position": v(-4.2, -10.5) * mm});
            skLineSegment(sketch, "E86.0.2.28", {"start": v(-7.41, -8.7) * mm, "end": v(-5.34, -8.7) * mm});
            skPoint(sketch, "E86.0.2.30", {"position": v(8.45, -10.5) * mm});
            skLineSegment(sketch, "E86.0.2.31", {"start": v(-16.45, -9.63) * mm, "end": v(-15.91, -8.7) * mm});
            skPoint(sketch, "E86.0.2.32", {"position": v(4.2, -10.5) * mm});
            skPoint(sketch, "E86.0.2.33", {"position": v(-12.8, -10.5) * mm});
            skLineSegment(sketch, "E86.0.2.34", {"start": v(-15.91, -12.3) * mm, "end": v(-16.6, -11.13) * mm});
            skPoint(sketch, "E86.0.2.35", {"position": v(12.7, -10.5) * mm});
            skPoint(sketch, "E86.0.2.36", {"position": v(-8.55, -10.5) * mm});
            skPoint(sketch, "E86.0.2.37", {"position": v(8.55, -10.5) * mm});
            skPoint(sketch, "E86.0.2.38", {"position": v(-14.95, -9.75) * mm});
            skLineSegment(sketch, "E86.0.2.39", {"start": v(-15.91, -8.7) * mm, "end": v(-13.84, -8.7) * mm});
            skLineSegment(sketch, "E86.0.2.40", {"start": v(-13.84, -12.3) * mm, "end": v(-15.91, -12.3) * mm});
            skLineSegment(sketch, "E86.0.2.41", {"start": v(-13.84, -8.7) * mm, "end": v(-13.23, -9.75) * mm});
            skLineSegment(sketch, "E86.0.2.42", {"start": v(12.27, -11.25) * mm, "end": v(11.66, -12.3) * mm});
            skLineSegment(sketch, "E86.0.2.43", {"start": v(-3.77, -11.25) * mm, "end": v(-4.73, -11.25) * mm});
            skLineSegment(sketch, "E86.0.2.44", {"start": v(-12.27, -11.25) * mm, "end": v(-13.24, -11.25) * mm});
            skLineSegment(sketch, "E86.0.2.45", {"start": v(7.41, -8.7) * mm, "end": v(8.02, -9.75) * mm});
            skLineSegment(sketch, "E86.0.2.46", {"start": v(-8.02, -9.75) * mm, "end": v(-7.41, -8.7) * mm});
            skLineSegment(sketch, "E86.0.2.47", {"start": v(-3.77, -9.75) * mm, "end": v(-3.16, -8.7) * mm});
            skLineSegment(sketch, "E86.0.2.48", {"start": v(13.23, -9.75) * mm, "end": v(12.27, -9.75) * mm});
            skLineSegment(sketch, "E86.0.2.49", {"start": v(0.48, -9.75) * mm, "end": v(-0.48, -9.75) * mm});
            skLineSegment(sketch, "E86.0.2.50", {"start": v(4.73, -9.75) * mm, "end": v(5.34, -8.7) * mm});
            skLineSegment(sketch, "E86.0.2.51", {"start": v(3.77, -11.25) * mm, "end": v(3.16, -12.3) * mm});
            skLineSegment(sketch, "E86.0.2.52", {"start": v(13.23, -11.25) * mm, "end": v(12.27, -11.25) * mm});
            skLineSegment(sketch, "E86.0.2.53", {"start": v(9.59, -12.3) * mm, "end": v(8.98, -11.25) * mm});
            skLineSegment(sketch, "E86.0.2.54", {"start": v(13.23, -9.75) * mm, "end": v(13.84, -8.7) * mm});
            skLineSegment(sketch, "E86.0.2.55", {"start": v(-8.02, -9.75) * mm, "end": v(-8.98, -9.75) * mm});
            skLineSegment(sketch, "E86.0.2.56", {"start": v(8.02, -11.25) * mm, "end": v(7.41, -12.3) * mm});
            skLineSegment(sketch, "E86.0.2.57", {"start": v(1.09, -12.3) * mm, "end": v(0.48, -11.25) * mm});
            skLineSegment(sketch, "E86.0.2.58", {"start": v(-11.66, -12.3) * mm, "end": v(-12.27, -11.25) * mm});
            skLineSegment(sketch, "E86.0.2.59", {"start": v(11.66, -8.7) * mm, "end": v(12.27, -9.75) * mm});
            skLineSegment(sketch, "E86.0.2.60", {"start": v(-8.02, -11.25) * mm, "end": v(-8.98, -11.25) * mm});
            skLineSegment(sketch, "E86.0.2.61", {"start": v(0.48, -11.25) * mm, "end": v(-0.48, -11.25) * mm});
            skLineSegment(sketch, "E86.0.2.62", {"start": v(3.16, -8.7) * mm, "end": v(3.77, -9.75) * mm});
            skLineSegment(sketch, "E86.0.2.63", {"start": v(0.48, -9.75) * mm, "end": v(1.09, -8.7) * mm});
            skLineSegment(sketch, "E86.0.2.64", {"start": v(-12.27, -9.75) * mm, "end": v(-11.66, -8.7) * mm});
            skLineSegment(sketch, "E86.0.2.65", {"start": v(4.73, -9.75) * mm, "end": v(3.77, -9.75) * mm});
            skLineSegment(sketch, "E86.0.2.66", {"start": v(13.84, -12.3) * mm, "end": v(13.23, -11.25) * mm});
            skLineSegment(sketch, "E86.0.2.67", {"start": v(-5.34, -8.7) * mm, "end": v(-4.73, -9.75) * mm});
            skLineSegment(sketch, "E86.0.2.68", {"start": v(-3.77, -9.75) * mm, "end": v(-4.73, -9.75) * mm});
            skLineSegment(sketch, "E86.0.2.69", {"start": v(-0.48, -11.25) * mm, "end": v(-1.09, -12.3) * mm});
            skLineSegment(sketch, "E86.0.2.70", {"start": v(8.98, -9.75) * mm, "end": v(9.59, -8.7) * mm});
            skLineSegment(sketch, "E86.0.2.71", {"start": v(5.34, -12.3) * mm, "end": v(4.73, -11.25) * mm});
            skLineSegment(sketch, "E86.0.2.72", {"start": v(-3.16, -12.3) * mm, "end": v(-3.77, -11.25) * mm});
            skLineSegment(sketch, "E86.0.2.73", {"start": v(-1.09, -8.7) * mm, "end": v(-0.48, -9.75) * mm});
            skLineSegment(sketch, "E86.0.2.74", {"start": v(4.73, -11.25) * mm, "end": v(3.77, -11.25) * mm});
            skLineSegment(sketch, "E86.0.2.75", {"start": v(-12.27, -9.75) * mm, "end": v(-13.24, -9.75) * mm});
            skLineSegment(sketch, "E86.0.2.76", {"start": v(-8.98, -11.25) * mm, "end": v(-9.59, -12.3) * mm});
            skLineSegment(sketch, "E86.0.2.77", {"start": v(-9.59, -8.7) * mm, "end": v(-8.98, -9.75) * mm});
            skLineSegment(sketch, "E86.0.2.78", {"start": v(8.98, -11.25) * mm, "end": v(8.02, -11.25) * mm});
            skLineSegment(sketch, "E86.0.2.79", {"start": v(-7.41, -12.3) * mm, "end": v(-8.02, -11.25) * mm});
            skLineSegment(sketch, "E86.0.2.80", {"start": v(-4.73, -11.25) * mm, "end": v(-5.34, -12.3) * mm});
            skLineSegment(sketch, "E86.0.2.81", {"start": v(-13.23, -11.25) * mm, "end": v(-13.84, -12.3) * mm});
            skLineSegment(sketch, "E86.0.2.82", {"start": v(8.98, -9.75) * mm, "end": v(8.02, -9.75) * mm});
            skLineSegment(sketch, "E86.direction1", {"start": v(-15.91, 9.2) * mm, "end": v(9.09, 9.2) * mm, "construction": true});
            skPoint(sketch, "E87.0.1.0", {"position": v(4.2, 4.5) * mm});
            skPoint(sketch, "E87.0.1.1", {"position": v(-12.7, -6.25) * mm});
            skPoint(sketch, "E87.0.1.2", {"position": v(-12.8, 4.5) * mm});
            skPoint(sketch, "E87.0.1.3", {"position": v(15.05, 3.75) * mm});
            skPoint(sketch, "E87.0.1.4", {"position": v(12.8, -6.25) * mm});
            skLineSegment(sketch, "E87.0.1.5", {"start": v(9.59, -4.45) * mm, "end": v(11.66, -4.45) * mm});
            skPoint(sketch, "E87.0.1.6", {"position": v(-14.88, -4.45) * mm});
            skPoint(sketch, "E87.0.1.7", {"position": v(-4.2, 4.5) * mm});
            skPoint(sketch, "E87.0.1.8", {"position": v(-8.45, -6.25) * mm});
            skLineSegment(sketch, "E87.0.1.9", {"start": v(11.66, 2.7) * mm, "end": v(9.59, 2.7) * mm});
            skPoint(sketch, "E87.0.1.10", {"position": v(-14.88, 6.3) * mm});
            skLineSegment(sketch, "E87.0.1.11", {"start": v(-3.16, -4.45) * mm, "end": v(-1.09, -4.45) * mm});
            skLineSegment(sketch, "E87.0.1.12", {"start": v(7.41, 2.7) * mm, "end": v(5.34, 2.7) * mm});
            skLineSegment(sketch, "E87.0.1.13", {"start": v(11.66, -8.05) * mm, "end": v(9.59, -8.05) * mm});
            skLineSegment(sketch, "E87.0.1.14", {"start": v(-3.16, 6.3) * mm, "end": v(-1.09, 6.3) * mm});
            skPoint(sketch, "E87.0.1.15", {"position": v(-8.55, 4.5) * mm});
            skPoint(sketch, "E87.0.1.16", {"position": v(8.45, -6.25) * mm});
            skLineSegment(sketch, "E87.0.1.17", {"start": v(-5.34, 2.7) * mm, "end": v(-7.41, 2.7) * mm});
            skLineSegment(sketch, "E87.0.1.18", {"start": v(-11.66, -4.45) * mm, "end": v(-9.59, -4.45) * mm});
            skPoint(sketch, "E87.0.1.19", {"position": v(-14.95, 5.25) * mm});
            skLineSegment(sketch, "E87.0.1.20", {"start": v(5.34, 6.3) * mm, "end": v(7.41, 6.3) * mm});
            skLineSegment(sketch, "E87.0.1.21", {"start": v(-7.41, -4.45) * mm, "end": v(-5.34, -4.45) * mm});
            skLineSegment(sketch, "E87.0.1.22", {"start": v(1.09, -4.45) * mm, "end": v(3.16, -4.45) * mm});
            skPoint(sketch, "E87.0.1.23", {"position": v(12.7, -6.25) * mm});
            skLineSegment(sketch, "E87.0.1.24", {"start": v(1.09, 6.3) * mm, "end": v(3.16, 6.3) * mm});
            skLineSegment(sketch, "E87.0.1.25", {"start": v(-7.41, 6.3) * mm, "end": v(-5.34, 6.3) * mm});
            skLineSegment(sketch, "E87.0.1.26", {"start": v(3.16, 2.7) * mm, "end": v(1.09, 2.7) * mm});
            skPoint(sketch, "E87.0.1.27", {"position": v(12.7, 4.5) * mm});
            skPoint(sketch, "E87.0.1.28", {"position": v(0.05, 4.5) * mm});
            skLineSegment(sketch, "E87.0.1.29", {"start": v(9.59, 6.3) * mm, "end": v(11.66, 6.3) * mm});
            skPoint(sketch, "E87.0.1.30", {"position": v(-4.2, -6.25) * mm});
            skLineSegment(sketch, "E87.0.1.31", {"start": v(-5.34, -8.05) * mm, "end": v(-7.41, -8.05) * mm});
            skPoint(sketch, "E87.0.1.32", {"position": v(-14.95, 3.75) * mm});
            skPoint(sketch, "E87.0.1.33", {"position": v(-14.95, -7) * mm});
            skLineSegment(sketch, "E87.0.1.34", {"start": v(-1.09, 2.7) * mm, "end": v(-3.16, 2.7) * mm});
            skPoint(sketch, "E87.0.1.35", {"position": v(8.55, 4.5) * mm});
            skPoint(sketch, "E87.0.1.36", {"position": v(4.2, -6.25) * mm});
            skLineSegment(sketch, "E87.0.1.37", {"start": v(-11.66, 6.3) * mm, "end": v(-9.59, 6.3) * mm});
            skPoint(sketch, "E87.0.1.38", {"position": v(-14.95, -5.5) * mm});
            skPoint(sketch, "E87.0.1.39", {"position": v(-0.05, -6.25) * mm});
            skLineSegment(sketch, "E87.0.1.40", {"start": v(5.34, -4.45) * mm, "end": v(7.41, -4.45) * mm});
            skLineSegment(sketch, "E87.0.1.41", {"start": v(-9.59, -8.05) * mm, "end": v(-11.66, -8.05) * mm});
            skPoint(sketch, "E87.0.1.42", {"position": v(15.05, -5.5) * mm});
            skLineSegment(sketch, "E87.0.1.43", {"start": v(-9.59, 2.7) * mm, "end": v(-11.66, 2.7) * mm});
            skLineSegment(sketch, "E87.0.1.44", {"start": v(7.41, -8.05) * mm, "end": v(5.34, -8.05) * mm});
            skLineSegment(sketch, "E87.0.1.45", {"start": v(3.16, -8.05) * mm, "end": v(1.09, -8.05) * mm});
            skPoint(sketch, "E87.0.1.46", {"position": v(15.05, 5.25) * mm});
            skLineSegment(sketch, "E87.0.1.47", {"start": v(-1.09, -8.05) * mm, "end": v(-3.16, -8.05) * mm});
            skPoint(sketch, "E87.0.1.48", {"position": v(15.05, -7) * mm});
            skPoint(sketch, "E87.0.1.49", {"position": v(12.8, 4.5) * mm});
            skLineSegment(sketch, "E87.0.1.50", {"start": v(13.84, 6.3) * mm, "end": v(15.91, 6.3) * mm});
            skPoint(sketch, "E87.0.1.51", {"position": v(-0.02, 4.65) * mm});
            skLineSegment(sketch, "E87.0.1.52", {"start": v(13.84, -4.45) * mm, "end": v(15.91, -4.45) * mm});
            skPoint(sketch, "E87.0.1.53", {"position": v(4.3, -6.25) * mm});
            skPoint(sketch, "E87.0.1.54", {"position": v(8.45, 4.5) * mm});
            skLineSegment(sketch, "E87.0.1.55", {"start": v(15.91, 2.7) * mm, "end": v(13.84, 2.7) * mm});
            skLineSegment(sketch, "E87.0.1.56", {"start": v(15.91, -8.05) * mm, "end": v(13.84, -8.05) * mm});
            skPoint(sketch, "E87.0.1.57", {"position": v(-4.3, -6.25) * mm});
            skPoint(sketch, "E87.0.1.58", {"position": v(4.3, 4.5) * mm});
            skPoint(sketch, "E87.0.1.59", {"position": v(-12.7, 4.5) * mm});
            skPoint(sketch, "E87.0.1.60", {"position": v(-12.8, -6.25) * mm});
            skPoint(sketch, "E87.0.1.61", {"position": v(0.05, -6.25) * mm});
            skCircle(sketch, "E87.0.1.62", {"center": v(-14.88, -6.25) * mm, "radius": 1.8 * mm, "construction": true});
            skPoint(sketch, "E87.0.1.63", {"position": v(-4.3, 4.5) * mm});
            skPoint(sketch, "E87.0.1.64", {"position": v(8.55, -6.25) * mm});
            skCircle(sketch, "E87.0.1.65", {"center": v(-14.88, 4.5) * mm, "radius": 1.8 * mm, "construction": true});
            skPoint(sketch, "E87.0.1.66", {"position": v(-8.55, -6.25) * mm});
            skPoint(sketch, "E87.0.1.67", {"position": v(-8.45, 4.5) * mm});
            skLineSegment(sketch, "E87.0.1.68", {"start": v(16.95, -6.25) * mm, "end": v(15.91, -8.05) * mm});
            skLineSegment(sketch, "E87.0.1.69", {"start": v(7.41, -4.45) * mm, "end": v(8.02, -5.5) * mm});
            skLineSegment(sketch, "E87.0.1.70", {"start": v(0.48, 5.25) * mm, "end": v(1.09, 6.3) * mm});
            skLineSegment(sketch, "E87.0.1.71", {"start": v(15.91, 6.3) * mm, "end": v(16.95, 4.5) * mm});
            skLineSegment(sketch, "E87.0.1.72", {"start": v(0.48, -7) * mm, "end": v(-0.48, -7) * mm});
            skLineSegment(sketch, "E87.0.1.73", {"start": v(-7.41, -8.05) * mm, "end": v(-8.02, -7) * mm});
            skLineSegment(sketch, "E87.0.1.74", {"start": v(-9.59, -4.45) * mm, "end": v(-8.98, -5.5) * mm});
            skLineSegment(sketch, "E87.0.1.75", {"start": v(-12.27, 3.75) * mm, "end": v(-13.24, 3.75) * mm});
            skLineSegment(sketch, "E87.0.1.76", {"start": v(-8.02, 3.75) * mm, "end": v(-8.98, 3.75) * mm});
            skLineSegment(sketch, "E87.0.1.77", {"start": v(-8.98, 3.75) * mm, "end": v(-9.59, 2.7) * mm});
            skLineSegment(sketch, "E87.0.1.78", {"start": v(3.16, -4.45) * mm, "end": v(3.77, -5.5) * mm});
            skLineSegment(sketch, "E87.0.1.79", {"start": v(-8.02, -5.5) * mm, "end": v(-7.41, -4.45) * mm});
            skLineSegment(sketch, "E87.0.1.80", {"start": v(0.48, -5.5) * mm, "end": v(1.09, -4.45) * mm});
            skLineSegment(sketch, "E87.0.1.81", {"start": v(-12.27, -5.5) * mm, "end": v(-11.66, -4.45) * mm});
            skLineSegment(sketch, "E87.0.1.82", {"start": v(16.95, 4.5) * mm, "end": v(15.91, 2.7) * mm});
            skLineSegment(sketch, "E87.0.1.83", {"start": v(-3.77, 5.25) * mm, "end": v(-3.16, 6.3) * mm});
            skLineSegment(sketch, "E87.0.1.84", {"start": v(-4.73, -7) * mm, "end": v(-5.34, -8.05) * mm});
            skLineSegment(sketch, "E87.0.1.85", {"start": v(-7.41, 2.7) * mm, "end": v(-8.02, 3.75) * mm});
            skLineSegment(sketch, "E87.0.1.86", {"start": v(-3.77, -5.5) * mm, "end": v(-3.16, -4.45) * mm});
            skLineSegment(sketch, "E87.0.1.87", {"start": v(15.91, -4.45) * mm, "end": v(16.95, -6.25) * mm});
            skLineSegment(sketch, "E87.0.1.88", {"start": v(8.98, -7) * mm, "end": v(8.02, -7) * mm});
            skLineSegment(sketch, "E87.0.1.89", {"start": v(3.16, 6.3) * mm, "end": v(3.77, 5.25) * mm});
            skLineSegment(sketch, "E87.0.1.90", {"start": v(-8.02, 5.25) * mm, "end": v(-7.41, 6.3) * mm});
            skLineSegment(sketch, "E87.0.1.91", {"start": v(-9.59, 6.3) * mm, "end": v(-8.98, 5.25) * mm});
            skLineSegment(sketch, "E87.0.1.92", {"start": v(0.48, 3.75) * mm, "end": v(-0.48, 3.75) * mm});
            skLineSegment(sketch, "E87.0.1.93", {"start": v(7.41, 6.3) * mm, "end": v(8.02, 5.25) * mm});
            skLineSegment(sketch, "E87.0.1.94", {"start": v(13.23, -5.5) * mm, "end": v(12.27, -5.5) * mm});
            skLineSegment(sketch, "E87.0.1.95", {"start": v(-12.27, -7) * mm, "end": v(-13.24, -7) * mm});
            skLineSegment(sketch, "E87.0.1.96", {"start": v(-8.02, -7) * mm, "end": v(-8.98, -7) * mm});
            skLineSegment(sketch, "E87.0.1.97", {"start": v(-8.98, -7) * mm, "end": v(-9.59, -8.05) * mm});
            skLineSegment(sketch, "E87.0.1.98", {"start": v(-3.77, 3.75) * mm, "end": v(-4.73, 3.75) * mm});
            skLineSegment(sketch, "E87.0.1.99", {"start": v(11.66, 6.3) * mm, "end": v(12.27, 5.25) * mm});
            skLineSegment(sketch, "E87.0.1.100", {"start": v(-12.27, 5.25) * mm, "end": v(-13.24, 5.25) * mm});
            skLineSegment(sketch, "E87.0.1.101", {"start": v(-1.09, 6.3) * mm, "end": v(-0.48, 5.25) * mm});
            skLineSegment(sketch, "E87.0.1.102", {"start": v(12.27, -7) * mm, "end": v(11.66, -8.05) * mm});
            skLineSegment(sketch, "E87.0.1.103", {"start": v(-11.66, -8.05) * mm, "end": v(-12.27, -7) * mm});
            skLineSegment(sketch, "E87.0.1.104", {"start": v(-13.84, 6.3) * mm, "end": v(-13.23, 5.25) * mm});
            skLineSegment(sketch, "E87.0.1.105", {"start": v(1.09, 2.7) * mm, "end": v(0.48, 3.75) * mm});
            skLineSegment(sketch, "E87.0.1.106", {"start": v(-12.27, -5.5) * mm, "end": v(-13.24, -5.5) * mm});
            skLineSegment(sketch, "E87.0.1.107", {"start": v(4.73, 3.75) * mm, "end": v(3.77, 3.75) * mm});
            skLineSegment(sketch, "E87.0.1.108", {"start": v(-3.77, -7) * mm, "end": v(-4.73, -7) * mm});
            skLineSegment(sketch, "E87.0.1.109", {"start": v(11.66, -4.45) * mm, "end": v(12.27, -5.5) * mm});
            skLineSegment(sketch, "E87.0.1.110", {"start": v(12.27, 3.75) * mm, "end": v(11.66, 2.7) * mm});
            skLineSegment(sketch, "E87.0.1.111", {"start": v(-11.66, 2.7) * mm, "end": v(-12.27, 3.75) * mm});
            skLineSegment(sketch, "E87.0.1.112", {"start": v(0.48, 5.25) * mm, "end": v(-0.48, 5.25) * mm});
            skLineSegment(sketch, "E87.0.1.113", {"start": v(4.73, -5.5) * mm, "end": v(5.34, -4.45) * mm});
            skLineSegment(sketch, "E87.0.1.114", {"start": v(-13.23, 3.75) * mm, "end": v(-13.84, 2.7) * mm});
            skLineSegment(sketch, "E87.0.1.115", {"start": v(4.73, 5.25) * mm, "end": v(3.77, 5.25) * mm});
            skLineSegment(sketch, "E87.0.1.116", {"start": v(8.98, -5.5) * mm, "end": v(8.02, -5.5) * mm});
            skLineSegment(sketch, "E87.0.1.117", {"start": v(13.84, -8.05) * mm, "end": v(13.23, -7) * mm});
            skLineSegment(sketch, "E87.0.1.118", {"start": v(3.77, 3.75) * mm, "end": v(3.16, 2.7) * mm});
            skLineSegment(sketch, "E87.0.1.119", {"start": v(-5.34, 6.3) * mm, "end": v(-4.73, 5.25) * mm});
            skLineSegment(sketch, "E87.0.1.120", {"start": v(-3.77, -5.5) * mm, "end": v(-4.73, -5.5) * mm});
            skLineSegment(sketch, "E87.0.1.121", {"start": v(13.23, 3.75) * mm, "end": v(12.27, 3.75) * mm});
            skLineSegment(sketch, "E87.0.1.122", {"start": v(-3.77, 5.25) * mm, "end": v(-4.73, 5.25) * mm});
            skLineSegment(sketch, "E87.0.1.123", {"start": v(9.59, 2.7) * mm, "end": v(8.98, 3.75) * mm});
            skLineSegment(sketch, "E87.0.1.124", {"start": v(-16.95, 4.5) * mm, "end": v(-15.91, 6.3) * mm});
            skLineSegment(sketch, "E87.0.1.125", {"start": v(13.23, -5.5) * mm, "end": v(13.84, -4.45) * mm});
            skLineSegment(sketch, "E87.0.1.126", {"start": v(-15.91, -8.05) * mm, "end": v(-16.95, -6.25) * mm});
            skLineSegment(sketch, "E87.0.1.127", {"start": v(-4.73, 3.75) * mm, "end": v(-5.34, 2.7) * mm});
            skLineSegment(sketch, "E87.0.1.128", {"start": v(-8.02, -5.5) * mm, "end": v(-8.98, -5.5) * mm});
            skLineSegment(sketch, "E87.0.1.129", {"start": v(-12.27, 5.25) * mm, "end": v(-11.66, 6.3) * mm});
            skLineSegment(sketch, "E87.0.1.130", {"start": v(13.23, 5.25) * mm, "end": v(12.27, 5.25) * mm});
            skLineSegment(sketch, "E87.0.1.131", {"start": v(-13.23, -7) * mm, "end": v(-13.84, -8.05) * mm});
            skLineSegment(sketch, "E87.0.1.132", {"start": v(0.48, -5.5) * mm, "end": v(-0.48, -5.5) * mm});
            skLineSegment(sketch, "E87.0.1.133", {"start": v(-15.91, -4.45) * mm, "end": v(-13.84, -4.45) * mm});
            skLineSegment(sketch, "E87.0.1.134", {"start": v(8.98, 5.25) * mm, "end": v(9.59, 6.3) * mm});
            skLineSegment(sketch, "E87.0.1.135", {"start": v(5.34, -8.05) * mm, "end": v(4.73, -7) * mm});
            skLineSegment(sketch, "E87.0.1.136", {"start": v(13.23, 5.25) * mm, "end": v(13.84, 6.3) * mm});
            skLineSegment(sketch, "E87.0.1.137", {"start": v(-15.91, 2.7) * mm, "end": v(-16.95, 4.5) * mm});
            skLineSegment(sketch, "E87.0.1.138", {"start": v(4.73, 5.25) * mm, "end": v(5.34, 6.3) * mm});
            skLineSegment(sketch, "E87.0.1.139", {"start": v(-3.16, -8.05) * mm, "end": v(-3.77, -7) * mm});
            skLineSegment(sketch, "E87.0.1.140", {"start": v(-8.02, 5.25) * mm, "end": v(-8.98, 5.25) * mm});
            skLineSegment(sketch, "E87.0.1.141", {"start": v(-15.91, 6.3) * mm, "end": v(-13.84, 6.3) * mm});
            skLineSegment(sketch, "E87.0.1.142", {"start": v(3.77, -7) * mm, "end": v(3.16, -8.05) * mm});
            skLineSegment(sketch, "E87.0.1.143", {"start": v(8.02, -7) * mm, "end": v(7.41, -8.05) * mm});
            skLineSegment(sketch, "E87.0.1.144", {"start": v(-13.84, -8.05) * mm, "end": v(-15.91, -8.05) * mm});
            skLineSegment(sketch, "E87.0.1.145", {"start": v(5.34, 2.7) * mm, "end": v(4.73, 3.75) * mm});
            skLineSegment(sketch, "E87.0.1.146", {"start": v(13.84, 2.7) * mm, "end": v(13.23, 3.75) * mm});
            skLineSegment(sketch, "E87.0.1.147", {"start": v(8.02, 3.75) * mm, "end": v(7.41, 2.7) * mm});
            skLineSegment(sketch, "E87.0.1.148", {"start": v(-13.84, 2.7) * mm, "end": v(-15.91, 2.7) * mm});
            skLineSegment(sketch, "E87.0.1.149", {"start": v(1.09, -8.05) * mm, "end": v(0.48, -7) * mm});
            skLineSegment(sketch, "E87.0.1.150", {"start": v(-13.84, -4.45) * mm, "end": v(-13.23, -5.5) * mm});
            skLineSegment(sketch, "E87.0.1.151", {"start": v(9.59, -8.05) * mm, "end": v(8.98, -7) * mm});
            skLineSegment(sketch, "E87.0.1.152", {"start": v(-16.95, -6.25) * mm, "end": v(-15.91, -4.45) * mm});
            skLineSegment(sketch, "E87.0.1.153", {"start": v(-0.48, -7) * mm, "end": v(-1.09, -8.05) * mm});
            skLineSegment(sketch, "E87.0.1.154", {"start": v(-0.48, 3.75) * mm, "end": v(-1.09, 2.7) * mm});
            skLineSegment(sketch, "E87.0.1.155", {"start": v(8.98, -5.5) * mm, "end": v(9.59, -4.45) * mm});
            skLineSegment(sketch, "E87.0.1.156", {"start": v(-5.34, -4.45) * mm, "end": v(-4.73, -5.5) * mm});
            skLineSegment(sketch, "E87.0.1.157", {"start": v(-3.16, 2.7) * mm, "end": v(-3.77, 3.75) * mm});
            skLineSegment(sketch, "E87.0.1.158", {"start": v(-1.09, -4.45) * mm, "end": v(-0.48, -5.5) * mm});
            skLineSegment(sketch, "E87.0.1.159", {"start": v(8.98, 3.75) * mm, "end": v(8.02, 3.75) * mm});
            skLineSegment(sketch, "E87.0.1.160", {"start": v(4.73, -7) * mm, "end": v(3.77, -7) * mm});
            skLineSegment(sketch, "E87.0.1.161", {"start": v(13.23, -7) * mm, "end": v(12.27, -7) * mm});
            skLineSegment(sketch, "E87.0.1.162", {"start": v(4.73, -5.5) * mm, "end": v(3.77, -5.5) * mm});
            skLineSegment(sketch, "E87.0.1.163", {"start": v(8.98, 5.25) * mm, "end": v(8.02, 5.25) * mm});
            skLineSegment(sketch, "E87.direction1", {"start": v(-15.91, -12.3) * mm, "end": v(9.09, -12.3) * mm, "construction": true});
            skLineSegment(sketch, "E87.direction2", {"start": v(-15.91, -12.3) * mm, "end": v(-15.91, -8.05) * mm, "construction": true});
            skArc(sketch, "E88", {"start": v(-17.42, 11.13) * mm, "mid": v(-20.75, 10.38) * mm, "end": v(-17.42, 9.62) * mm});
            skCircle(sketch, "E89", {"center": v(-27.9, 0) * mm, "radius": 2 * mm});
            skArc(sketch, "E90.MirrorC", {"start": v(17.42, 11.12) * mm, "mid": v(20.75, 10.38) * mm, "end": v(17.42, 9.62) * mm});
            skArc(sketch, "E91.MirrorC", {"start": v(17.42, -11.13) * mm, "mid": v(20.75, -10.38) * mm, "end": v(17.42, -9.62) * mm});
            skArc(sketch, "E92.MirrorC", {"start": v(-17.42, -11.13) * mm, "mid": v(-20.75, -10.38) * mm, "end": v(-17.42, -9.62) * mm});
            skCircle(sketch, "E93.MirrorC", {"center": v(27.9, 0) * mm, "radius": 2 * mm});
            skLineSegment(sketch, "E94.bottom", {"start": v(23.48, -14.6) * mm, "end": v(-23.52, -14.6) * mm});
            skLineSegment(sketch, "E94.top", {"start": v(23.48, 15.4) * mm, "end": v(-23.52, 15.4) * mm});
            skLineSegment(sketch, "E94.left", {"start": v(23.48, -14.6) * mm, "end": v(23.48, -6.5) * mm});
            skLineSegment(sketch, "E94.right", {"start": v(-23.52, -14.6) * mm, "end": v(-23.52, -6.5) * mm});
            skArc(sketch, "E95", {"start": v(-30.73, 3.5) * mm, "mid": v(-32.4, 0) * mm, "end": v(-30.73, -3.5) * mm});
            skLineSegment(sketch, "E96", {"start": v(-30.73, 3.5) * mm, "end": v(-26.52, 3.5) * mm});
            skLineSegment(sketch, "E97.trimOffspring", {"start": v(-13.38, 3.5) * mm, "end": v(-13.37, 3.5) * mm});
            skLineSegment(sketch, "E98.trimOffspring", {"start": v(26.48, 3.5) * mm, "end": v(30.73, 3.5) * mm});
            skLineSegment(sketch, "E99", {"start": v(-30.73, -3.5) * mm, "end": v(-26.52, -3.5) * mm});
            skLineSegment(sketch, "E100.trimOffspring", {"start": v(26.48, -3.5) * mm, "end": v(30.73, -3.5) * mm});
            skArc(sketch, "E101.trimOffspring", {"start": v(30.73, -3.5) * mm, "mid": v(32.4, 0) * mm, "end": v(30.73, 3.5) * mm});
            skLineSegment(sketch, "E102.trimOffspring", {"start": v(23.48, 6.5) * mm, "end": v(23.48, 15.4) * mm});
            skLineSegment(sketch, "E103.trimOffspring", {"start": v(-23.52, 6.5) * mm, "end": v(-23.52, 15.4) * mm});
            skPoint(sketch, "E104.visualSharp", {"position": v(-23.52, 3.5) * mm});
            skArc(sketch, "E104.filletArc", {"start": v(-26.52, 3.5) * mm, "mid": v(-24.4, 4.38) * mm, "end": v(-23.52, 6.5) * mm});
            skPoint(sketch, "E105.visualSharp", {"position": v(-23.52, -3.5) * mm});
            skArc(sketch, "E105.filletArc", {"start": v(-23.52, -6.5) * mm, "mid": v(-24.4, -4.38) * mm, "end": v(-26.52, -3.5) * mm});
            skPoint(sketch, "E106.visualSharp", {"position": v(23.48, -3.5) * mm});
            skArc(sketch, "E106.filletArc", {"start": v(26.48, -3.5) * mm, "mid": v(24.35, -4.38) * mm, "end": v(23.48, -6.5) * mm});
            skPoint(sketch, "E107.visualSharp", {"position": v(23.48, 3.5) * mm});
            skArc(sketch, "E107.filletArc", {"start": v(23.48, 6.5) * mm, "mid": v(24.35, 4.38) * mm, "end": v(26.48, 3.5) * mm});
            skLineSegment(sketch, "E108", {"start": v(-17.42, 11.13) * mm, "end": v(-16.88, 11.13) * mm});
            skLineSegment(sketch, "E109", {"start": v(-17.42, 9.62) * mm, "end": v(-16.16, 9.62) * mm});
            skPoint(sketch, "E110.orphan", {"position": v(-16.95, 11) * mm});
            skLineSegment(sketch, "E111", {"start": v(16.16, 9.62) * mm, "end": v(17.42, 9.62) * mm});
            skPoint(sketch, "E111.startSnap0", {"position": v(-16.79, 9.62) * mm});
            skLineSegment(sketch, "E112", {"start": v(16.88, 11.12) * mm, "end": v(17.42, 11.12) * mm});
            skPoint(sketch, "E113.orphan", {"position": v(16.95, 11) * mm});
            skLineSegment(sketch, "E114", {"start": v(16.45, -9.62) * mm, "end": v(17.42, -9.62) * mm});
            skLineSegment(sketch, "E115", {"start": v(16.6, -11.13) * mm, "end": v(17.42, -11.13) * mm});
            skPoint(sketch, "E116.orphan", {"position": v(16.95, -10.5) * mm});
            skLineSegment(sketch, "E117", {"start": v(-17.42, -9.62) * mm, "end": v(-16.45, -9.62) * mm});
            skLineSegment(sketch, "E118", {"start": v(-17.42, -11.13) * mm, "end": v(-16.6, -11.13) * mm});
            skPoint(sketch, "E119.orphan", {"position": v(-16.95, -10.5) * mm});
            skSolve(sketch);
        }
        {
            var Q0;
            Q0=makeQuery(id+"F2.imprint","IMPRINT",FACE,{"disambiguationData":[TD([[makeQuery(id+"F2.imprint","IMPRINT",EDGE,{"derivedFrom":sQuery(id+"F2.wireOp",EDGE,"E56.0")}),1.0]])]});
            extrude(context, id + "F3", {"entities" : qUnion([Q0]), "depth" : 4 * mm});
        }
        {
            var Q0;
            Q0=makeQuery(id+"F0.imprint","IMPRINT",FACE,{"disambiguationData":[TD([[makeQuery(id+"F0.imprint","IMPRINT",EDGE,{"derivedFrom":sQuery(id+"F0.wireOp",EDGE,"E0")}),-1.0]])]});
            extrude(context, id + "F4", {"entities" : qUnion([Q0]), "depth" : 3.1 * mm});
        }
        {
            var Q0;
            Q0 = qSketchRegion(id + "F1", true);
            extrude(context, id + "F5", {"entities" : qUnion([Q0]), "operationType" : NewBodyOperationType.REMOVE, "depth" : 25 * mm});
        }
        {
            var Q0;
            Q0=makeQuery(id+"F4.opExtrude","SWEPT_EDGE",EDGE,{"disambiguationData":[OSD([sQuery(id+"F0.wireOp",EDGE,"E18.MirrorCS"),sQuery(id+"F0.wireOp",EDGE,"E19.MirrorCS")])]});
            var Q1;
            Q1=makeQuery(id+"F4.opExtrude","SWEPT_EDGE",EDGE,{"disambiguationData":[OSD([sQuery(id+"F0.wireOp",EDGE,"E16.MirrorCS"),sQuery(id+"F0.wireOp",EDGE,"E17.MirrorCS")])]});
            var Q2;
            Q2=makeQuery(id+"F4.opExtrude","SWEPT_EDGE",EDGE,{"disambiguationData":[OSD([sQuery(id+"F0.wireOp",EDGE,"E14.MirrorCS"),sQuery(id+"F0.wireOp",EDGE,"E15.MirrorCS")])]});
            var Q3;
            Q3=makeQuery(id+"F4.opExtrude","SWEPT_EDGE",EDGE,{"disambiguationData":[OSD([sQuery(id+"F0.wireOp",EDGE,"E12"),sQuery(id+"F0.wireOp",EDGE,"E13")])]});
            var Q4;
            Q4=makeQuery(id+"F4.opExtrude","SWEPT_EDGE",EDGE,{"disambiguationData":[OSD([sQuery(id+"F0.wireOp",EDGE,"E11.left"),sQuery(id+"F0.wireOp",EDGE,"E15.MirrorCS")])]});
            var Q5;
            Q5=makeQuery(id+"F4.opExtrude","SWEPT_EDGE",EDGE,{"disambiguationData":[OSD([sQuery(id+"F0.wireOp",EDGE,"E11.left"),sQuery(id+"F0.wireOp",EDGE,"E16.MirrorCS")])]});
            var Q6;
            Q6=makeQuery(id+"F4.opExtrude","SWEPT_EDGE",EDGE,{"disambiguationData":[OSD([sQuery(id+"F0.wireOp",EDGE,"E11.right"),sQuery(id+"F0.wireOp",EDGE,"E12")])]});
            var Q7;
            Q7=makeQuery(id+"F4.opExtrude","SWEPT_EDGE",EDGE,{"disambiguationData":[OSD([sQuery(id+"F0.wireOp",EDGE,"E11.right"),sQuery(id+"F0.wireOp",EDGE,"E18.MirrorCS")])]});
            chamfer(context, id + "F6", {"entities" : qUnion([Q0, Q1, Q2, Q3, Q4, Q5, Q6, Q7]), "width" : 2 * mm, "tangentPropagation" : true});
        }
    });
